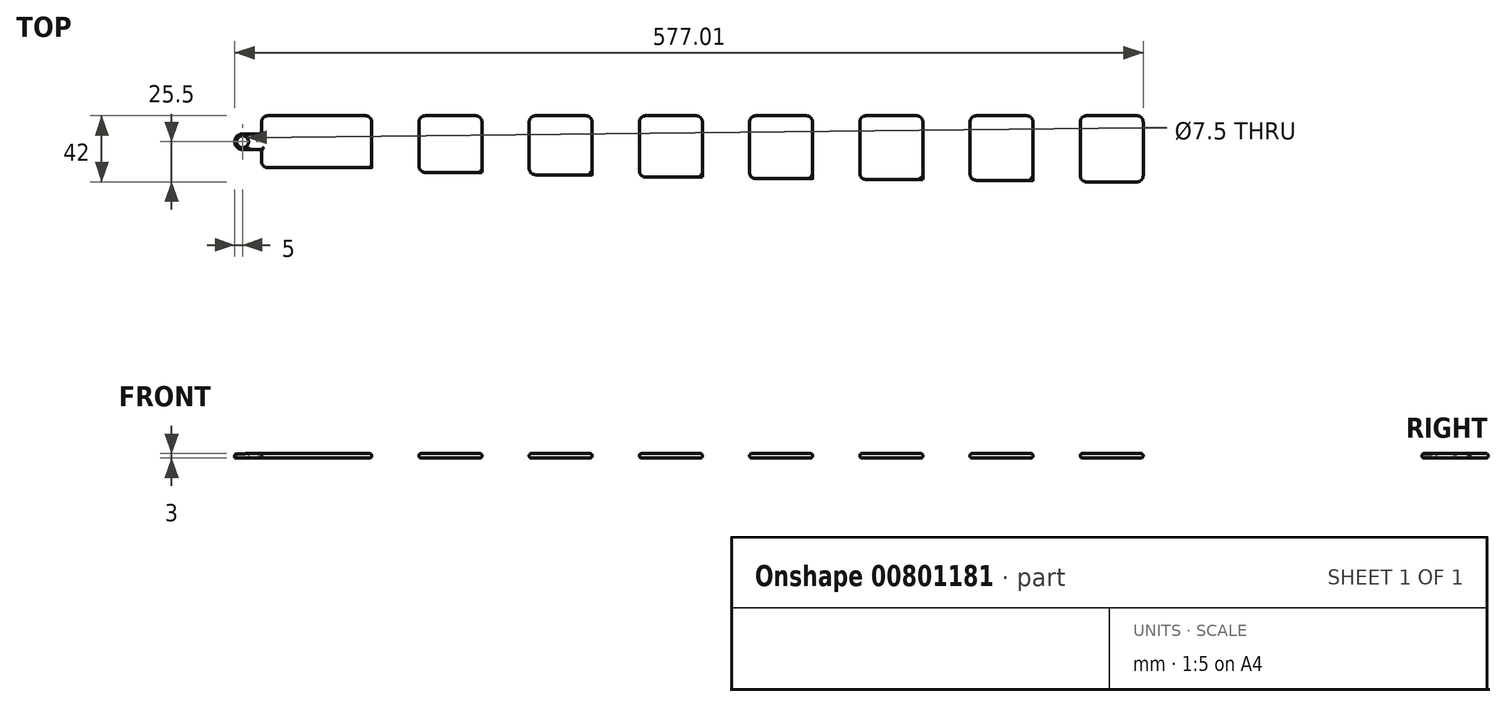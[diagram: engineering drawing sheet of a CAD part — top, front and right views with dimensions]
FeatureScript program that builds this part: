
annotation { "Feature Type Name" : "Feature", "Feature Type Description" : "" }
export const myFeature = defineFeature(function(context is Context, id is Id, definition is map)
    precondition{}
    {
        {
            var Q0;
            Q0=qCreatedBy(makeId("Top.planeOp"),FACE);
            var sketch = newSketch(context, id + "F0", { "sketchPlane" : qUnion([Q0])});
            skLineSegment(sketch, "E0.top", {"start": v(560, 0) * mm, "end": v(490, 0) * mm});
            skLineSegment(sketch, "E0.right", {"start": v(490, 1) * mm, "end": v(490, 0) * mm});
            skLineSegment(sketch, "E1.top", {"start": v(490, 1) * mm, "end": v(420, 1) * mm});
            skLineSegment(sketch, "E1.right", {"start": v(420, 1.5) * mm, "end": v(420, 1) * mm});
            skLineSegment(sketch, "E2.top", {"start": v(420, 1.5) * mm, "end": v(350, 1.5) * mm});
            skLineSegment(sketch, "E2.right", {"start": v(350, 2) * mm, "end": v(350, 1.5) * mm});
            skLineSegment(sketch, "E3.top", {"start": v(350, 2) * mm, "end": v(280, 2) * mm});
            skLineSegment(sketch, "E3.right", {"start": v(280, 3) * mm, "end": v(280, 2) * mm});
            skLineSegment(sketch, "E4.top", {"start": v(280, 3) * mm, "end": v(210, 3) * mm});
            skLineSegment(sketch, "E4.right", {"start": v(210, 4.5) * mm, "end": v(210, 3) * mm});
            skLineSegment(sketch, "E5.top", {"start": v(210, 4.5) * mm, "end": v(140, 4.5) * mm});
            skLineSegment(sketch, "E5.right", {"start": v(140, 6) * mm, "end": v(140, 4.5) * mm});
            skLineSegment(sketch, "E6", {"start": v(70, 6) * mm, "end": v(140, 6) * mm});
            skLineSegment(sketch, "E7", {"start": v(560, 0) * mm, "end": v(490, 0) * mm, "construction": true});
            skLineSegment(sketch, "E8.top", {"start": v(70, 9) * mm, "end": v(0, 9) * mm});
            skLineSegment(sketch, "E8.left", {"start": v(70, 6) * mm, "end": v(70, 9) * mm});
            skText(sketch, "E9", { "text": "9.0 6.0 4.5 3.0 2.0 1.5 1.0 0.0", "fontName": "RobotoSlab-Bold.ttf"});
            skLineSegment(sketch, "E10.bottom", {"start": v(560, 0) * mm, "end": v(0, 0) * mm, "construction": true});
            skLineSegment(sketch, "E10.left", {"start": v(560, 0) * mm, "end": v(560, 42) * mm});
            skLineSegment(sketch, "E10.right", {"start": v(0, 9) * mm, "end": v(0, 42) * mm});
            skPoint(sketch, "E11", {"position": v(-22.14, 43.86) * mm});
            skPoint(sketch, "E12", {"position": v(560, 21) * mm});
            skLineSegment(sketch, "E13.bottom", {"start": v(70, 9) * mm, "end": v(30, 9) * mm});
            skLineSegment(sketch, "E13.top", {"start": v(70, 42) * mm, "end": v(30, 42) * mm});
            skLineSegment(sketch, "E13.left", {"start": v(70, 9) * mm, "end": v(70, 42) * mm});
            skLineSegment(sketch, "E13.right", {"start": v(30, 9) * mm, "end": v(30, 42) * mm});
            skLineSegment(sketch, "E14.bottom", {"start": v(140, 6) * mm, "end": v(100, 6) * mm});
            skLineSegment(sketch, "E14.top", {"start": v(140, 42) * mm, "end": v(100, 42) * mm});
            skLineSegment(sketch, "E14.left", {"start": v(140, 6) * mm, "end": v(140, 42) * mm});
            skLineSegment(sketch, "E14.right", {"start": v(100, 6) * mm, "end": v(100, 42) * mm});
            skLineSegment(sketch, "E15.bottom", {"start": v(210, 4.5) * mm, "end": v(170, 4.5) * mm});
            skLineSegment(sketch, "E15.top", {"start": v(210, 42) * mm, "end": v(170, 42) * mm});
            skLineSegment(sketch, "E15.left", {"start": v(210, 4.5) * mm, "end": v(210, 42) * mm});
            skLineSegment(sketch, "E15.right", {"start": v(170, 4.5) * mm, "end": v(170, 42) * mm});
            skLineSegment(sketch, "E16.bottom", {"start": v(280, 3) * mm, "end": v(240, 3) * mm});
            skLineSegment(sketch, "E16.top", {"start": v(280, 42) * mm, "end": v(240, 42) * mm});
            skLineSegment(sketch, "E16.left", {"start": v(280, 3) * mm, "end": v(280, 42) * mm});
            skLineSegment(sketch, "E16.right", {"start": v(240, 3) * mm, "end": v(240, 42) * mm});
            skLineSegment(sketch, "E17.bottom", {"start": v(350, 2) * mm, "end": v(310, 2) * mm});
            skLineSegment(sketch, "E17.top", {"start": v(350, 42) * mm, "end": v(310, 42) * mm});
            skLineSegment(sketch, "E17.left", {"start": v(350, 2) * mm, "end": v(350, 42) * mm});
            skLineSegment(sketch, "E17.right", {"start": v(310, 2) * mm, "end": v(310, 42) * mm});
            skLineSegment(sketch, "E18.bottom", {"start": v(420, 1.5) * mm, "end": v(380, 1.5) * mm});
            skLineSegment(sketch, "E18.top", {"start": v(420, 42) * mm, "end": v(380, 42) * mm});
            skLineSegment(sketch, "E18.left", {"start": v(420, 1.5) * mm, "end": v(420, 42) * mm});
            skLineSegment(sketch, "E18.right", {"start": v(380, 1.5) * mm, "end": v(380, 42) * mm});
            skLineSegment(sketch, "E19.bottom", {"start": v(490, 1) * mm, "end": v(450, 1) * mm});
            skLineSegment(sketch, "E19.top", {"start": v(490, 42) * mm, "end": v(450, 42) * mm});
            skLineSegment(sketch, "E19.left", {"start": v(490, 1) * mm, "end": v(490, 42) * mm});
            skLineSegment(sketch, "E19.right", {"start": v(450, 1) * mm, "end": v(450, 42) * mm});
            skLineSegment(sketch, "E20", {"start": v(0, 42) * mm, "end": v(560, 42) * mm});
            skLineSegment(sketch, "E21.bottom", {"start": v(560, 0) * mm, "end": v(520, 0) * mm});
            skLineSegment(sketch, "E21.top", {"start": v(560, 42) * mm, "end": v(520, 42) * mm});
            skLineSegment(sketch, "E21.right", {"start": v(520, 0) * mm, "end": v(520, 42) * mm});
            const initialGuessF0  = {"E9": [-0.25714, 0.0371, 1, 0, 0.01354]};
            skSetInitialGuess(sketch, initialGuessF0);
            skSolve(sketch);
        }
        {
            var Q0;
            Q0=makeQuery(id+"F0.imprint","IMPRINT",FACE,{"disambiguationData":[TD([[makeQuery(id+"F0.imprint","IMPRINT",EDGE,{"derivedFrom":sQuery(id+"F0.wireOp",EDGE,"E8.top")}),-1.0]])]});
            var Q1;
            Q1=makeQuery(id+"F0.imprint","IMPRINT",FACE,{"disambiguationData":[TD([[makeQuery(id+"F0.imprint","IMPRINT",EDGE,{"derivedFrom":sQuery(id+"F0.wireOp",EDGE,"E6")}),1.0]])]});
            var Q2;
            Q2=makeQuery(id+"F0.imprint","IMPRINT",FACE,{"disambiguationData":[TD([[makeQuery(id+"F0.imprint","IMPRINT",EDGE,{"derivedFrom":sQuery(id+"F0.wireOp",EDGE,"E5.top")}),-1.0]])]});
            var Q3;
            Q3=makeQuery(id+"F0.imprint","IMPRINT",FACE,{"disambiguationData":[TD([[makeQuery(id+"F0.imprint","IMPRINT",EDGE,{"derivedFrom":sQuery(id+"F0.wireOp",EDGE,"E4.top")}),-1.0]])]});
            var Q4;
            Q4=makeQuery(id+"F0.imprint","IMPRINT",FACE,{"disambiguationData":[TD([[makeQuery(id+"F0.imprint","IMPRINT",EDGE,{"derivedFrom":sQuery(id+"F0.wireOp",EDGE,"E3.top")}),-1.0]])]});
            var Q5;
            Q5=makeQuery(id+"F0.imprint","IMPRINT",FACE,{"disambiguationData":[TD([[makeQuery(id+"F0.imprint","IMPRINT",EDGE,{"derivedFrom":sQuery(id+"F0.wireOp",EDGE,"E2.top")}),-1.0]])]});
            var Q6;
            Q6=makeQuery(id+"F0.imprint","IMPRINT",FACE,{"disambiguationData":[TD([[makeQuery(id+"F0.imprint","IMPRINT",EDGE,{"derivedFrom":sQuery(id+"F0.wireOp",EDGE,"E1.top")}),-1.0]])]});
            var Q7;
            Q7=makeQuery(id+"F0.imprint","IMPRINT",FACE,{"disambiguationData":[TD([[makeQuery(id+"F0.imprint","IMPRINT",EDGE,{"derivedFrom":sQuery(id+"F0.wireOp",EDGE,"E0.top")}),-1.0]])]});
            extrude(context, id + "F1", {"entities" : qUnion([Q0, Q1, Q2, Q3, Q4, Q5, Q6, Q7]), "depth" : 3 * mm, "offsetDistance" : 25 * mm});
        }
        {
            var Q0;
            Q0=makeQuery(id+"F1.opExtrude","CAP_FACE",FACE,{"disambiguationData":[OSD([sQuery(id+"F0.wireOp",EDGE,"E8.top"),sQuery(id+"F0.wireOp",EDGE,"E10.right"),sQuery(id+"F0.wireOp",EDGE,"E13.right"),sQuery(id+"F0.wireOp",EDGE,"E20")])],"isStart":false});
            var sketch = newSketch(context, id + "F2", { "sketchPlane" : qUnion([Q0])});
            skLineSegment(sketch, "E22.bottom", {"start": v(0, 30.5) * mm, "end": v(-12, 30.5) * mm});
            skLineSegment(sketch, "E22.top", {"start": v(0, 20.5) * mm, "end": v(-12, 20.5) * mm});
            skLineSegment(sketch, "E22.left", {"start": v(0, 30.5) * mm, "end": v(0, 20.5) * mm});
            skLineSegment(sketch, "E22.right", {"start": v(-17, 25.5) * mm, "end": v(-17, 25.5) * mm});
            skPoint(sketch, "E23", {"position": v(0, 25.5) * mm});
            skPoint(sketch, "E24.visualSharp", {"position": v(-17, 30.5) * mm});
            skArc(sketch, "E24.filletArc", {"start": v(-12, 30.5) * mm, "mid": v(-15.55, 29.04) * mm, "end": v(-17, 25.5) * mm});
            skPoint(sketch, "E25.visualSharp", {"position": v(-17, 20.5) * mm});
            skArc(sketch, "E25.filletArc", {"start": v(-17, 25.5) * mm, "mid": v(-15.55, 21.96) * mm, "end": v(-12, 20.5) * mm});
            skCircle(sketch, "E26", {"center": v(-12, 25.5) * mm, "radius": 3.75 * mm});
            skLineSegment(sketch, "E27.bottom", {"start": v(70, 29) * mm, "end": v(57.42, 29) * mm});
            skLineSegment(sketch, "E27.top", {"start": v(70, 19) * mm, "end": v(57.42, 19) * mm});
            skLineSegment(sketch, "E27.left", {"start": v(70, 29) * mm, "end": v(70, 19) * mm});
            skLineSegment(sketch, "E27.right", {"start": v(52.42, 24) * mm, "end": v(52.42, 24) * mm});
            skPoint(sketch, "E28", {"position": v(70, 24) * mm});
            skPoint(sketch, "E29.visualSharp", {"position": v(52.42, 29) * mm});
            skArc(sketch, "E29.filletArc", {"start": v(57.42, 29) * mm, "mid": v(53.88, 27.54) * mm, "end": v(52.42, 24) * mm});
            skPoint(sketch, "E30.visualSharp", {"position": v(52.42, 19) * mm});
            skArc(sketch, "E30.filletArc", {"start": v(52.42, 24) * mm, "mid": v(53.88, 20.46) * mm, "end": v(57.42, 19) * mm});
            skCircle(sketch, "E31", {"center": v(57.42, 24) * mm, "radius": 3.75 * mm});
            skLineSegment(sketch, "E32.bottom", {"start": v(140, 28.25) * mm, "end": v(128, 28.25) * mm});
            skLineSegment(sketch, "E32.top", {"start": v(140, 18.25) * mm, "end": v(128, 18.25) * mm});
            skLineSegment(sketch, "E32.left", {"start": v(140, 28.25) * mm, "end": v(140, 18.25) * mm});
            skLineSegment(sketch, "E32.right", {"start": v(123, 23.25) * mm, "end": v(123, 23.25) * mm});
            skPoint(sketch, "E33", {"position": v(140, 23.25) * mm});
            skPoint(sketch, "E34.visualSharp", {"position": v(123, 28.25) * mm});
            skArc(sketch, "E34.filletArc", {"start": v(128, 28.25) * mm, "mid": v(124.45, 26.79) * mm, "end": v(123, 23.25) * mm});
            skPoint(sketch, "E35.visualSharp", {"position": v(123, 18.25) * mm});
            skArc(sketch, "E35.filletArc", {"start": v(123, 23.25) * mm, "mid": v(124.45, 19.71) * mm, "end": v(128, 18.25) * mm});
            skCircle(sketch, "E36", {"center": v(128, 23.25) * mm, "radius": 3.75 * mm});
            skLineSegment(sketch, "E37.bottom", {"start": v(210, 27.5) * mm, "end": v(198, 27.5) * mm});
            skLineSegment(sketch, "E37.top", {"start": v(210, 17.5) * mm, "end": v(198, 17.5) * mm});
            skLineSegment(sketch, "E37.left", {"start": v(210, 27.5) * mm, "end": v(210, 17.5) * mm});
            skLineSegment(sketch, "E37.right", {"start": v(193, 22.5) * mm, "end": v(193, 22.5) * mm});
            skPoint(sketch, "E38", {"position": v(210, 22.5) * mm});
            skPoint(sketch, "E39.visualSharp", {"position": v(193, 27.5) * mm});
            skArc(sketch, "E39.filletArc", {"start": v(198, 27.5) * mm, "mid": v(194.45, 26.04) * mm, "end": v(193, 22.5) * mm});
            skPoint(sketch, "E40.visualSharp", {"position": v(193, 17.5) * mm});
            skArc(sketch, "E40.filletArc", {"start": v(193, 22.5) * mm, "mid": v(194.45, 18.96) * mm, "end": v(198, 17.5) * mm});
            skCircle(sketch, "E41", {"center": v(198, 22.5) * mm, "radius": 3.75 * mm});
            skLineSegment(sketch, "E42.bottom", {"start": v(280, 27) * mm, "end": v(268, 27) * mm});
            skLineSegment(sketch, "E42.top", {"start": v(280, 17) * mm, "end": v(268, 17) * mm});
            skLineSegment(sketch, "E42.left", {"start": v(280, 27) * mm, "end": v(280, 17) * mm});
            skLineSegment(sketch, "E42.right", {"start": v(263, 22) * mm, "end": v(263, 22) * mm});
            skPoint(sketch, "E43", {"position": v(280, 22) * mm});
            skPoint(sketch, "E44.visualSharp", {"position": v(263, 27) * mm});
            skArc(sketch, "E44.filletArc", {"start": v(268, 27) * mm, "mid": v(264.45, 25.54) * mm, "end": v(263, 22) * mm});
            skPoint(sketch, "E45.visualSharp", {"position": v(263, 17) * mm});
            skArc(sketch, "E45.filletArc", {"start": v(263, 22) * mm, "mid": v(264.45, 18.46) * mm, "end": v(268, 17) * mm});
            skCircle(sketch, "E46", {"center": v(268, 22) * mm, "radius": 3.75 * mm});
            skLineSegment(sketch, "E47.bottom", {"start": v(350, 26.75) * mm, "end": v(338, 26.75) * mm});
            skLineSegment(sketch, "E47.top", {"start": v(350, 16.75) * mm, "end": v(338, 16.75) * mm});
            skLineSegment(sketch, "E47.left", {"start": v(350, 26.75) * mm, "end": v(350, 16.75) * mm});
            skLineSegment(sketch, "E47.right", {"start": v(333, 21.75) * mm, "end": v(333, 21.75) * mm});
            skPoint(sketch, "E48", {"position": v(350, 21.75) * mm});
            skPoint(sketch, "E49.visualSharp", {"position": v(333, 26.75) * mm});
            skArc(sketch, "E49.filletArc", {"start": v(338, 26.75) * mm, "mid": v(334.45, 25.29) * mm, "end": v(333, 21.75) * mm});
            skPoint(sketch, "E50.visualSharp", {"position": v(333, 16.75) * mm});
            skArc(sketch, "E50.filletArc", {"start": v(333, 21.75) * mm, "mid": v(334.45, 18.21) * mm, "end": v(338, 16.75) * mm});
            skCircle(sketch, "E51", {"center": v(338, 21.75) * mm, "radius": 3.75 * mm});
            skLineSegment(sketch, "E52.bottom", {"start": v(420, 26.5) * mm, "end": v(408, 26.5) * mm});
            skLineSegment(sketch, "E52.top", {"start": v(420, 16.5) * mm, "end": v(408, 16.5) * mm});
            skLineSegment(sketch, "E52.left", {"start": v(420, 26.5) * mm, "end": v(420, 16.5) * mm});
            skLineSegment(sketch, "E52.right", {"start": v(403, 21.5) * mm, "end": v(403, 21.5) * mm});
            skPoint(sketch, "E53", {"position": v(420, 21.5) * mm});
            skPoint(sketch, "E54.visualSharp", {"position": v(403, 26.5) * mm});
            skArc(sketch, "E54.filletArc", {"start": v(408, 26.5) * mm, "mid": v(404.45, 25.04) * mm, "end": v(403, 21.5) * mm});
            skPoint(sketch, "E55.visualSharp", {"position": v(403, 16.5) * mm});
            skArc(sketch, "E55.filletArc", {"start": v(403, 21.5) * mm, "mid": v(404.45, 17.96) * mm, "end": v(408, 16.5) * mm});
            skCircle(sketch, "E56", {"center": v(408, 21.5) * mm, "radius": 3.75 * mm});
            skLineSegment(sketch, "E57.bottom", {"start": v(490, 26) * mm, "end": v(478, 26) * mm});
            skLineSegment(sketch, "E57.top", {"start": v(490, 16) * mm, "end": v(478, 16) * mm});
            skLineSegment(sketch, "E57.left", {"start": v(490, 26) * mm, "end": v(490, 16) * mm});
            skLineSegment(sketch, "E57.right", {"start": v(473, 21) * mm, "end": v(473, 21) * mm});
            skPoint(sketch, "E58", {"position": v(490, 21) * mm});
            skPoint(sketch, "E59.visualSharp", {"position": v(473, 26) * mm});
            skArc(sketch, "E59.filletArc", {"start": v(478, 26) * mm, "mid": v(474.45, 24.54) * mm, "end": v(473, 21) * mm});
            skPoint(sketch, "E60.visualSharp", {"position": v(473, 16) * mm});
            skArc(sketch, "E60.filletArc", {"start": v(473, 21) * mm, "mid": v(474.45, 17.46) * mm, "end": v(478, 16) * mm});
            skCircle(sketch, "E61", {"center": v(478, 21) * mm, "radius": 3.75 * mm});
            skSolve(sketch);
        }
        {
            var Q0;
            Q0 = qSketchRegion(id + "F2", true);
            var Q1;
            Q1=makeQuery(id+"F1.opExtrude","CAP_FACE",FACE,{"disambiguationData":[OSD([sQuery(id+"F0.wireOp",EDGE,"E8.top"),sQuery(id+"F0.wireOp",EDGE,"E10.right"),sQuery(id+"F0.wireOp",EDGE,"E13.right"),sQuery(id+"F0.wireOp",EDGE,"E20")])],"isStart":true});
            extrude(context, id + "F3", {"entities" : qUnion([Q0]), "operationType" : NewBodyOperationType.ADD, "endBound" : BoundingType.UP_TO_SURFACE, "oppositeDirection" : true, "depth" : 25 * mm, "endBoundEntityFace" : qUnion([Q1]), "offsetDistance" : 25 * mm});
        }
        {
            var Q0;
            Q0=makeQuery(id+"F1.opExtrude","SWEPT_EDGE",EDGE,{"disambiguationData":[OSD([sQuery(id+"F0.wireOp",EDGE,"E10.right"),sQuery(id+"F0.wireOp",EDGE,"E20")])]});
            var Q1;
            Q1=makeQuery(id+"F1.opExtrude","SWEPT_EDGE",EDGE,{"disambiguationData":[OSD([sQuery(id+"F0.wireOp",EDGE,"E13.right"),sQuery(id+"F0.wireOp",EDGE,"E20")])]});
            var Q2;
            Q2=makeQuery(id+"F1.opExtrude","SWEPT_EDGE",EDGE,{"disambiguationData":[OSD([sQuery(id+"F0.wireOp",EDGE,"E8.top"),sQuery(id+"F0.wireOp",EDGE,"E10.right")])]});
            var Q3;
            Q3=makeQuery(id+"F1.opExtrude","SWEPT_EDGE",EDGE,{"disambiguationData":[OSD([sQuery(id+"F0.wireOp",EDGE,"E8.top"),sQuery(id+"F0.wireOp",EDGE,"E13.bottom"),sQuery(id+"F0.wireOp",EDGE,"E13.right")])]});
            var Q4;
            Q4=makeQuery(id+"F1.opExtrude","SWEPT_EDGE",EDGE,{"disambiguationData":[OSD([sQuery(id+"F0.wireOp",EDGE,"E13.left"),sQuery(id+"F0.wireOp",EDGE,"E20")])]});
            var Q5;
            Q5=makeQuery(id+"F1.opExtrude","SWEPT_EDGE",EDGE,{"disambiguationData":[OSD([sQuery(id+"F0.wireOp",EDGE,"E14.left"),sQuery(id+"F0.wireOp",EDGE,"E20")])]});
            var Q6;
            Q6=makeQuery(id+"F1.opExtrude","SWEPT_EDGE",EDGE,{"disambiguationData":[OSD([sQuery(id+"F0.wireOp",EDGE,"E19.left"),sQuery(id+"F0.wireOp",EDGE,"E20")])]});
            var Q7;
            Q7=makeQuery(id+"F1.opExtrude","SWEPT_EDGE",EDGE,{"disambiguationData":[OSD([sQuery(id+"F0.wireOp",EDGE,"E18.left"),sQuery(id+"F0.wireOp",EDGE,"E20")])]});
            var Q8;
            Q8=makeQuery(id+"F1.opExtrude","SWEPT_EDGE",EDGE,{"disambiguationData":[OSD([sQuery(id+"F0.wireOp",EDGE,"E17.left"),sQuery(id+"F0.wireOp",EDGE,"E20")])]});
            var Q9;
            Q9=makeQuery(id+"F1.opExtrude","SWEPT_EDGE",EDGE,{"disambiguationData":[OSD([sQuery(id+"F0.wireOp",EDGE,"E16.left"),sQuery(id+"F0.wireOp",EDGE,"E20")])]});
            var Q10;
            Q10=makeQuery(id+"F1.opExtrude","SWEPT_EDGE",EDGE,{"disambiguationData":[OSD([sQuery(id+"F0.wireOp",EDGE,"E15.left"),sQuery(id+"F0.wireOp",EDGE,"E20")])]});
            var Q11;
            Q11=makeQuery(id+"F1.opExtrude","SWEPT_EDGE",EDGE,{"disambiguationData":[OSD([sQuery(id+"F0.wireOp",EDGE,"E20"),sQuery(id+"F0.wireOp",EDGE,"E21.top"),sQuery(id+"F0.wireOp",EDGE,"E21.right")])]});
            var Q12;
            Q12=makeQuery(id+"F1.opExtrude","SWEPT_EDGE",EDGE,{"disambiguationData":[OSD([sQuery(id+"F0.wireOp",EDGE,"E19.right"),sQuery(id+"F0.wireOp",EDGE,"E20")])]});
            var Q13;
            Q13=makeQuery(id+"F1.opExtrude","SWEPT_EDGE",EDGE,{"disambiguationData":[OSD([sQuery(id+"F0.wireOp",EDGE,"E18.right"),sQuery(id+"F0.wireOp",EDGE,"E20")])]});
            var Q14;
            Q14=makeQuery(id+"F1.opExtrude","SWEPT_EDGE",EDGE,{"disambiguationData":[OSD([sQuery(id+"F0.wireOp",EDGE,"E17.right"),sQuery(id+"F0.wireOp",EDGE,"E20")])]});
            var Q15;
            Q15=makeQuery(id+"F1.opExtrude","SWEPT_EDGE",EDGE,{"disambiguationData":[OSD([sQuery(id+"F0.wireOp",EDGE,"E16.right"),sQuery(id+"F0.wireOp",EDGE,"E20")])]});
            var Q16;
            Q16=makeQuery(id+"F1.opExtrude","SWEPT_EDGE",EDGE,{"disambiguationData":[OSD([sQuery(id+"F0.wireOp",EDGE,"E15.right"),sQuery(id+"F0.wireOp",EDGE,"E20")])]});
            var Q17;
            Q17=makeQuery(id+"F1.opExtrude","SWEPT_EDGE",EDGE,{"disambiguationData":[OSD([sQuery(id+"F0.wireOp",EDGE,"E14.right"),sQuery(id+"F0.wireOp",EDGE,"E20")])]});
            var Q18;
            Q18=makeQuery(id+"F1.opExtrude","SWEPT_EDGE",EDGE,{"disambiguationData":[OSD([sQuery(id+"F0.wireOp",EDGE,"E6"),sQuery(id+"F0.wireOp",EDGE,"E14.bottom"),sQuery(id+"F0.wireOp",EDGE,"E14.right")])]});
            var Q19;
            Q19=makeQuery(id+"F1.opExtrude","SWEPT_EDGE",EDGE,{"disambiguationData":[OSD([sQuery(id+"F0.wireOp",EDGE,"E5.top"),sQuery(id+"F0.wireOp",EDGE,"E15.bottom"),sQuery(id+"F0.wireOp",EDGE,"E15.right")])]});
            var Q20;
            Q20=makeQuery(id+"F1.opExtrude","SWEPT_EDGE",EDGE,{"disambiguationData":[OSD([sQuery(id+"F0.wireOp",EDGE,"E4.top"),sQuery(id+"F0.wireOp",EDGE,"E16.bottom"),sQuery(id+"F0.wireOp",EDGE,"E16.right")])]});
            var Q21;
            Q21=makeQuery(id+"F1.opExtrude","SWEPT_EDGE",EDGE,{"disambiguationData":[OSD([sQuery(id+"F0.wireOp",EDGE,"E3.top"),sQuery(id+"F0.wireOp",EDGE,"E17.bottom"),sQuery(id+"F0.wireOp",EDGE,"E17.right")])]});
            var Q22;
            Q22=makeQuery(id+"F1.opExtrude","SWEPT_EDGE",EDGE,{"disambiguationData":[OSD([sQuery(id+"F0.wireOp",EDGE,"E2.top"),sQuery(id+"F0.wireOp",EDGE,"E18.bottom"),sQuery(id+"F0.wireOp",EDGE,"E18.right")])]});
            var Q23;
            Q23=makeQuery(id+"F1.opExtrude","SWEPT_EDGE",EDGE,{"disambiguationData":[OSD([sQuery(id+"F0.wireOp",EDGE,"E1.top"),sQuery(id+"F0.wireOp",EDGE,"E19.bottom"),sQuery(id+"F0.wireOp",EDGE,"E19.right")])]});
            var Q24;
            Q24=makeQuery(id+"F1.opExtrude","SWEPT_EDGE",EDGE,{"disambiguationData":[OSD([sQuery(id+"F0.wireOp",EDGE,"E0.top"),sQuery(id+"F0.wireOp",EDGE,"E21.bottom"),sQuery(id+"F0.wireOp",EDGE,"E21.right")])]});
            var Q25;
            Q25=makeQuery(id+"F1.opExtrude","SWEPT_EDGE",EDGE,{"disambiguationData":[OSD([sQuery(id+"F0.wireOp",EDGE,"E6"),sQuery(id+"F0.wireOp",EDGE,"E8.left")])]});
            var Q26;
            Q26=makeQuery(id+"F1.opExtrude","SWEPT_EDGE",EDGE,{"disambiguationData":[OSD([sQuery(id+"F0.wireOp",EDGE,"E5.top"),sQuery(id+"F0.wireOp",EDGE,"E5.right")])]});
            var Q27;
            Q27=makeQuery(id+"F1.opExtrude","SWEPT_EDGE",EDGE,{"disambiguationData":[OSD([sQuery(id+"F0.wireOp",EDGE,"E4.top"),sQuery(id+"F0.wireOp",EDGE,"E4.right")])]});
            var Q28;
            Q28=makeQuery(id+"F1.opExtrude","SWEPT_EDGE",EDGE,{"disambiguationData":[OSD([sQuery(id+"F0.wireOp",EDGE,"E3.top"),sQuery(id+"F0.wireOp",EDGE,"E3.right")])]});
            var Q29;
            Q29=makeQuery(id+"F1.opExtrude","SWEPT_EDGE",EDGE,{"disambiguationData":[OSD([sQuery(id+"F0.wireOp",EDGE,"E2.top"),sQuery(id+"F0.wireOp",EDGE,"E2.right")])]});
            var Q30;
            Q30=makeQuery(id+"F1.opExtrude","SWEPT_EDGE",EDGE,{"disambiguationData":[OSD([sQuery(id+"F0.wireOp",EDGE,"E1.top"),sQuery(id+"F0.wireOp",EDGE,"E1.right")])]});
            var Q31;
            Q31=makeQuery(id+"F1.opExtrude","SWEPT_EDGE",EDGE,{"disambiguationData":[OSD([sQuery(id+"F0.wireOp",EDGE,"E0.top"),sQuery(id+"F0.wireOp",EDGE,"E0.right")])]});
            fillet(context, id + "F4", {"entities" : qUnion([Q0, Q1, Q2, Q3, Q4, Q5, Q6, Q7, Q8, Q9, Q10, Q11, Q12, Q13, Q14, Q15, Q16, Q17, Q18, Q19, Q20, Q21, Q22, Q23, Q24, Q25, Q26, Q27, Q28, Q29, Q30, Q31]), "radius" : 4 * mm, "tangentPropagation" : true, "allowEdgeOverflow" : false});
        }
        {
            var Q0;
            {var subQ1=sQuery(id+"F0.wireOp",EDGE,"E18.left");var subQ2=sQuery(id+"F0.wireOp",EDGE,"E1.right");var subQ3=sQuery(id+"F0.wireOp",EDGE,"E1.top");Q0=makeQuery(id+"F3.boolean.opBoolean","SPLIT",EDGE,{"disambiguationData":[TD([makeQuery(id+"F1.opExtrude","SWEPT_FACE",FACE,{"disambiguationData":[OSD([subQ3])]})])],"derivedFrom":makeQuery(id+"F1.opExtrude","CAP_EDGE",EDGE,{"disambiguationData":[OSD([subQ2,subQ1])],"isStart":false})});}
            var Q1;
            Q1=makeQuery(id+"F3.opExtrude","CAP_EDGE",EDGE,{"disambiguationData":[OSD([sQuery(id+"F2.wireOp",EDGE,"E54.filletArc"),sQuery(id+"F2.wireOp",EDGE,"E55.filletArc")])],"isStart":true});
            var Q2;
            Q2=makeQuery(id+"F3.opExtrude","CAP_EDGE",EDGE,{"disambiguationData":[OSD([sQuery(id+"F2.wireOp",EDGE,"E34.filletArc"),sQuery(id+"F2.wireOp",EDGE,"E35.filletArc")])],"isStart":true});
            var Q3;
            {var subQ1=sQuery(id+"F0.wireOp",EDGE,"E5.top");var subQ2=sQuery(id+"F0.wireOp",EDGE,"E14.left");var subQ3=sQuery(id+"F0.wireOp",EDGE,"E5.right");Q3=makeQuery(id+"F3.boolean.opBoolean","SPLIT",EDGE,{"disambiguationData":[TD([makeQuery(id+"F1.opExtrude","SWEPT_FACE",FACE,{"disambiguationData":[OSD([subQ1])]})])],"derivedFrom":makeQuery(id+"F1.opExtrude","CAP_EDGE",EDGE,{"disambiguationData":[OSD([subQ3,subQ2])],"isStart":false})});}
            var Q4;
            {var subQ1=sQuery(id+"F0.wireOp",EDGE,"E17.left");var subQ2=sQuery(id+"F0.wireOp",EDGE,"E2.right");var subQ3=sQuery(id+"F0.wireOp",EDGE,"E2.top");Q4=makeQuery(id+"F3.boolean.opBoolean","SPLIT",EDGE,{"disambiguationData":[TD([makeQuery(id+"F1.opExtrude","SWEPT_FACE",FACE,{"disambiguationData":[OSD([subQ3])]})])],"derivedFrom":makeQuery(id+"F1.opExtrude","CAP_EDGE",EDGE,{"disambiguationData":[OSD([subQ2,subQ1])],"isStart":false})});}
            var Q5;
            Q5=makeQuery(id+"F3.opExtrude","CAP_EDGE",EDGE,{"disambiguationData":[OSD([sQuery(id+"F2.wireOp",EDGE,"E59.filletArc"),sQuery(id+"F2.wireOp",EDGE,"E60.filletArc")])],"isStart":true});
            var Q6;
            {var subQ1=sQuery(id+"F0.wireOp",EDGE,"E19.left");var subQ2=sQuery(id+"F0.wireOp",EDGE,"E0.right");var subQ3=sQuery(id+"F0.wireOp",EDGE,"E0.top");Q6=makeQuery(id+"F3.boolean.opBoolean","SPLIT",EDGE,{"disambiguationData":[TD([makeQuery(id+"F1.opExtrude","SWEPT_FACE",FACE,{"disambiguationData":[OSD([subQ3])]})])],"derivedFrom":makeQuery(id+"F1.opExtrude","CAP_EDGE",EDGE,{"disambiguationData":[OSD([subQ2,subQ1])],"isStart":false})});}
            var Q7;
            {var subQ1=sQuery(id+"F0.wireOp",EDGE,"E13.left");var subQ2=sQuery(id+"F0.wireOp",EDGE,"E8.left");var subQ3=sQuery(id+"F0.wireOp",EDGE,"E6");Q7=makeQuery(id+"F3.boolean.opBoolean","SPLIT",EDGE,{"disambiguationData":[TD([makeQuery(id+"F1.opExtrude","SWEPT_FACE",FACE,{"disambiguationData":[OSD([subQ3])]})])],"derivedFrom":makeQuery(id+"F1.opExtrude","CAP_EDGE",EDGE,{"disambiguationData":[OSD([subQ2,subQ1])],"isStart":false})});}
            var Q8;
            Q8=makeQuery(id+"F3.opExtrude","CAP_EDGE",EDGE,{"disambiguationData":[OSD([sQuery(id+"F2.wireOp",EDGE,"E39.filletArc"),sQuery(id+"F2.wireOp",EDGE,"E40.filletArc")])],"isStart":true});
            var Q9;
            {var subQ1=sQuery(id+"F0.wireOp",EDGE,"E15.left");var subQ2=sQuery(id+"F0.wireOp",EDGE,"E4.right");var subQ3=sQuery(id+"F0.wireOp",EDGE,"E4.top");Q9=makeQuery(id+"F3.boolean.opBoolean","SPLIT",EDGE,{"disambiguationData":[TD([makeQuery(id+"F1.opExtrude","SWEPT_FACE",FACE,{"disambiguationData":[OSD([subQ3])]})])],"derivedFrom":makeQuery(id+"F1.opExtrude","CAP_EDGE",EDGE,{"disambiguationData":[OSD([subQ2,subQ1])],"isStart":false})});}
            var Q10;
            Q10=makeQuery(id+"F3.opExtrude","CAP_EDGE",EDGE,{"disambiguationData":[OSD([sQuery(id+"F2.wireOp",EDGE,"E24.filletArc"),sQuery(id+"F2.wireOp",EDGE,"E25.filletArc")])],"isStart":true});
            var Q11;
            {var subQ1=sQuery(id+"F0.wireOp",EDGE,"E16.left");var subQ2=sQuery(id+"F0.wireOp",EDGE,"E3.right");var subQ3=sQuery(id+"F0.wireOp",EDGE,"E3.top");Q11=makeQuery(id+"F3.boolean.opBoolean","SPLIT",EDGE,{"disambiguationData":[TD([makeQuery(id+"F1.opExtrude","SWEPT_FACE",FACE,{"disambiguationData":[OSD([subQ3])]})])],"derivedFrom":makeQuery(id+"F1.opExtrude","CAP_EDGE",EDGE,{"disambiguationData":[OSD([subQ2,subQ1])],"isStart":false})});}
            var Q12;
            Q12=makeQuery(id+"F1.opExtrude","CAP_EDGE",EDGE,{"disambiguationData":[OSD([sQuery(id+"F0.wireOp",EDGE,"E19.right")])],"isStart":false});
            var Q13;
            Q13=makeQuery(id+"F1.opExtrude","SWEPT_EDGE",EDGE,{"disambiguationData":[OSD([sQuery(id+"F0.wireOp",EDGE,"E1.top"),sQuery(id+"F0.wireOp",EDGE,"E1.right")])]});
            var Q14;
            {var subQ0=sQuery(id+"F0.wireOp",EDGE,"E20");Q14=makeQuery(id+"F1.opExtrude","CAP_EDGE",EDGE,{"disambiguationData":[OSD([subQ0]),TDD([makeQuery(id+"F0.imprint","IMPRINT",EDGE,{"disambiguationData":[TD([[makeQuery(id+"F0.imprint","INTERSECT",VERTEX,{"derivedFrom":[sQuery(id+"F0.wireOp",EDGE,"E18.left"),subQ0]}),-1.0]])],"derivedFrom":subQ0})])],"isStart":false});}
            var Q15;
            Q15=makeQuery(id+"F3.opExtrude","SWEPT_EDGE",EDGE,{"disambiguationData":[OSD([sQuery(id+"F2.wireOp",EDGE,"E52.bottom"),sQuery(id+"F2.wireOp",EDGE,"E54.filletArc")])]});
            var Q16;
            Q16=makeQuery(id+"F3.opExtrude","CAP_EDGE",EDGE,{"disambiguationData":[OSD([sQuery(id+"F2.wireOp",EDGE,"E56")])],"isStart":true});
            var Q17;
            Q17=makeQuery(id+"F3.opExtrude","CAP_EDGE",EDGE,{"disambiguationData":[OSD([sQuery(id+"F2.wireOp",EDGE,"E52.top")])],"isStart":true});
            var Q18;
            {var subQ1=sQuery(id+"F0.wireOp",EDGE,"E18.left");var subQ3=sQuery(id+"F0.wireOp",EDGE,"E1.right");var subQ4=sQuery(id+"F2.wireOp",EDGE,"E52.bottom");Q18=makeQuery(id+"F3.boolean.opBoolean","SPLIT",EDGE,{"disambiguationData":[TD([makeQuery(id+"F3.opExtrude","SWEPT_FACE",FACE,{"disambiguationData":[OSD([subQ4])]})])],"derivedFrom":makeQuery(id+"F1.opExtrude","CAP_EDGE",EDGE,{"disambiguationData":[OSD([subQ3,subQ1])],"isStart":false})});}
            var Q19;
            Q19=makeQuery(id+"F3.opExtrude","CAP_EDGE",EDGE,{"disambiguationData":[OSD([sQuery(id+"F2.wireOp",EDGE,"E52.bottom")])],"isStart":true});
            var Q20;
            Q20=makeQuery(id+"F1.opExtrude","SWEPT_EDGE",EDGE,{"disambiguationData":[OSD([sQuery(id+"F0.wireOp",EDGE,"E5.top"),sQuery(id+"F0.wireOp",EDGE,"E5.right")])]});
            var Q21;
            {var subQ0=sQuery(id+"F0.wireOp",EDGE,"E20");Q21=makeQuery(id+"F1.opExtrude","CAP_EDGE",EDGE,{"disambiguationData":[OSD([subQ0]),TDD([makeQuery(id+"F0.imprint","IMPRINT",EDGE,{"disambiguationData":[TD([[makeQuery(id+"F0.imprint","INTERSECT",VERTEX,{"derivedFrom":[sQuery(id+"F0.wireOp",EDGE,"E14.left"),subQ0]}),-1.0]])],"derivedFrom":subQ0})])],"isStart":false});}
            var Q22;
            Q22=makeQuery(id+"F1.opExtrude","CAP_EDGE",EDGE,{"disambiguationData":[OSD([sQuery(id+"F0.wireOp",EDGE,"E5.top")])],"isStart":false});
            var Q23;
            Q23=makeQuery(id+"F1.opExtrude","CAP_EDGE",EDGE,{"disambiguationData":[OSD([sQuery(id+"F0.wireOp",EDGE,"E15.right")])],"isStart":false});
            var Q24;
            Q24=makeQuery(id+"F3.opExtrude","SWEPT_EDGE",EDGE,{"disambiguationData":[OSD([sQuery(id+"F2.wireOp",EDGE,"E32.top"),sQuery(id+"F2.wireOp",EDGE,"E35.filletArc")])]});
            var Q25;
            Q25=makeQuery(id+"F3.opExtrude","SWEPT_EDGE",EDGE,{"disambiguationData":[OSD([sQuery(id+"F2.wireOp",EDGE,"E32.bottom"),sQuery(id+"F2.wireOp",EDGE,"E34.filletArc")])]});
            var Q26;
            Q26=makeQuery(id+"F3.opExtrude","CAP_EDGE",EDGE,{"disambiguationData":[OSD([sQuery(id+"F2.wireOp",EDGE,"E32.top")])],"isStart":true});
            var Q27;
            {var subQ1=sQuery(id+"F0.wireOp",EDGE,"E14.left");var subQ3=sQuery(id+"F2.wireOp",EDGE,"E32.bottom");var subQ4=sQuery(id+"F0.wireOp",EDGE,"E5.right");Q27=makeQuery(id+"F3.boolean.opBoolean","SPLIT",EDGE,{"disambiguationData":[TD([makeQuery(id+"F3.opExtrude","SWEPT_FACE",FACE,{"disambiguationData":[OSD([subQ3])]})])],"derivedFrom":makeQuery(id+"F1.opExtrude","CAP_EDGE",EDGE,{"disambiguationData":[OSD([subQ4,subQ1])],"isStart":false})});}
            var Q28;
            Q28=makeQuery(id+"F3.opExtrude","CAP_EDGE",EDGE,{"disambiguationData":[OSD([sQuery(id+"F2.wireOp",EDGE,"E32.bottom")])],"isStart":true});
            var Q29;
            Q29=makeQuery(id+"F3.opExtrude","CAP_EDGE",EDGE,{"disambiguationData":[OSD([sQuery(id+"F2.wireOp",EDGE,"E36")])],"isStart":true});
            var Q30;
            Q30=makeQuery(id+"F1.opExtrude","CAP_EDGE",EDGE,{"disambiguationData":[OSD([sQuery(id+"F0.wireOp",EDGE,"E2.top")])],"isStart":false});
            var Q31;
            {var subQ0=sQuery(id+"F0.wireOp",EDGE,"E20");Q31=makeQuery(id+"F1.opExtrude","CAP_EDGE",EDGE,{"disambiguationData":[OSD([subQ0]),TDD([makeQuery(id+"F0.imprint","IMPRINT",EDGE,{"disambiguationData":[TD([[makeQuery(id+"F0.imprint","INTERSECT",VERTEX,{"derivedFrom":[sQuery(id+"F0.wireOp",EDGE,"E17.left"),subQ0]}),-1.0]])],"derivedFrom":subQ0})])],"isStart":false});}
            var Q32;
            Q32=makeQuery(id+"F1.opExtrude","CAP_EDGE",EDGE,{"disambiguationData":[OSD([sQuery(id+"F0.wireOp",EDGE,"E18.right")])],"isStart":false});
            var Q33;
            Q33=makeQuery(id+"F1.opExtrude","SWEPT_EDGE",EDGE,{"disambiguationData":[OSD([sQuery(id+"F0.wireOp",EDGE,"E2.top"),sQuery(id+"F0.wireOp",EDGE,"E2.right")])]});
            var Q34;
            Q34=makeQuery(id+"F3.opExtrude","CAP_EDGE",EDGE,{"disambiguationData":[OSD([sQuery(id+"F2.wireOp",EDGE,"E51")])],"isStart":true});
            var Q35;
            {var subQ1=sQuery(id+"F0.wireOp",EDGE,"E17.left");var subQ3=sQuery(id+"F0.wireOp",EDGE,"E2.right");var subQ4=sQuery(id+"F2.wireOp",EDGE,"E47.bottom");Q35=makeQuery(id+"F3.boolean.opBoolean","SPLIT",EDGE,{"disambiguationData":[TD([makeQuery(id+"F3.opExtrude","SWEPT_FACE",FACE,{"disambiguationData":[OSD([subQ4])]})])],"derivedFrom":makeQuery(id+"F1.opExtrude","CAP_EDGE",EDGE,{"disambiguationData":[OSD([subQ3,subQ1])],"isStart":false})});}
            var Q36;
            Q36=makeQuery(id+"F3.opExtrude","CAP_EDGE",EDGE,{"disambiguationData":[OSD([sQuery(id+"F2.wireOp",EDGE,"E49.filletArc"),sQuery(id+"F2.wireOp",EDGE,"E50.filletArc")])],"isStart":true});
            var Q37;
            Q37=makeQuery(id+"F3.opExtrude","CAP_EDGE",EDGE,{"disambiguationData":[OSD([sQuery(id+"F2.wireOp",EDGE,"E47.bottom")])],"isStart":true});
            var Q38;
            Q38=makeQuery(id+"F3.opExtrude","CAP_EDGE",EDGE,{"disambiguationData":[OSD([sQuery(id+"F2.wireOp",EDGE,"E47.top")])],"isStart":true});
            var Q39;
            Q39=makeQuery(id+"F1.opExtrude","SWEPT_EDGE",EDGE,{"disambiguationData":[OSD([sQuery(id+"F0.wireOp",EDGE,"E0.top"),sQuery(id+"F0.wireOp",EDGE,"E0.right")])]});
            var Q40;
            Q40=makeQuery(id+"F1.opExtrude","CAP_EDGE",EDGE,{"disambiguationData":[OSD([sQuery(id+"F0.wireOp",EDGE,"E21.right")])],"isStart":false});
            var Q41;
            {var subQ0=sQuery(id+"F0.wireOp",EDGE,"E20");Q41=makeQuery(id+"F1.opExtrude","CAP_EDGE",EDGE,{"disambiguationData":[OSD([subQ0]),TDD([makeQuery(id+"F0.imprint","IMPRINT",EDGE,{"disambiguationData":[TD([[makeQuery(id+"F0.imprint","INTERSECT",VERTEX,{"derivedFrom":[sQuery(id+"F0.wireOp",EDGE,"E19.left"),subQ0]}),-1.0]])],"derivedFrom":subQ0})])],"isStart":false});}
            var Q42;
            Q42=makeQuery(id+"F3.opExtrude","CAP_EDGE",EDGE,{"disambiguationData":[OSD([sQuery(id+"F2.wireOp",EDGE,"E61")])],"isStart":true});
            var Q43;
            Q43=makeQuery(id+"F3.opExtrude","CAP_EDGE",EDGE,{"disambiguationData":[OSD([sQuery(id+"F2.wireOp",EDGE,"E57.top")])],"isStart":true});
            var Q44;
            {var subQ1=sQuery(id+"F0.wireOp",EDGE,"E19.left");var subQ3=sQuery(id+"F0.wireOp",EDGE,"E0.right");var subQ4=sQuery(id+"F2.wireOp",EDGE,"E57.bottom");Q44=makeQuery(id+"F3.boolean.opBoolean","SPLIT",EDGE,{"disambiguationData":[TD([makeQuery(id+"F3.opExtrude","SWEPT_FACE",FACE,{"disambiguationData":[OSD([subQ4])]})])],"derivedFrom":makeQuery(id+"F1.opExtrude","CAP_EDGE",EDGE,{"disambiguationData":[OSD([subQ3,subQ1])],"isStart":false})});}
            var Q45;
            Q45=makeQuery(id+"F3.opExtrude","SWEPT_EDGE",EDGE,{"disambiguationData":[OSD([sQuery(id+"F2.wireOp",EDGE,"E57.top"),sQuery(id+"F2.wireOp",EDGE,"E60.filletArc")])]});
            var Q46;
            Q46=makeQuery(id+"F3.opExtrude","CAP_EDGE",EDGE,{"disambiguationData":[OSD([sQuery(id+"F2.wireOp",EDGE,"E57.bottom")])],"isStart":true});
            var Q47;
            Q47=makeQuery(id+"F3.opExtrude","CAP_EDGE",EDGE,{"disambiguationData":[OSD([sQuery(id+"F2.wireOp",EDGE,"E27.top")])],"isStart":true});
            var Q48;
            Q48=makeQuery(id+"F3.opExtrude","CAP_EDGE",EDGE,{"disambiguationData":[OSD([sQuery(id+"F2.wireOp",EDGE,"E29.filletArc"),sQuery(id+"F2.wireOp",EDGE,"E30.filletArc")])],"isStart":true});
            var Q49;
            Q49=makeQuery(id+"F1.opExtrude","SWEPT_EDGE",EDGE,{"disambiguationData":[OSD([sQuery(id+"F0.wireOp",EDGE,"E6"),sQuery(id+"F0.wireOp",EDGE,"E8.left")])]});
            var Q50;
            {var subQ0=sQuery(id+"F0.wireOp",EDGE,"E20");Q50=makeQuery(id+"F1.opExtrude","CAP_EDGE",EDGE,{"disambiguationData":[OSD([subQ0]),TDD([makeQuery(id+"F0.imprint","IMPRINT",EDGE,{"disambiguationData":[TD([[makeQuery(id+"F0.imprint","INTERSECT",VERTEX,{"derivedFrom":[sQuery(id+"F0.wireOp",EDGE,"E13.left"),subQ0]}),-1.0]])],"derivedFrom":subQ0})])],"isStart":false});}
            var Q51;
            Q51=makeQuery(id+"F1.opExtrude","CAP_EDGE",EDGE,{"disambiguationData":[OSD([sQuery(id+"F0.wireOp",EDGE,"E14.right")])],"isStart":false});
            var Q52;
            Q52=makeQuery(id+"F3.opExtrude","CAP_EDGE",EDGE,{"disambiguationData":[OSD([sQuery(id+"F2.wireOp",EDGE,"E31")])],"isStart":true});
            var Q53;
            Q53=makeQuery(id+"F3.opExtrude","CAP_EDGE",EDGE,{"disambiguationData":[OSD([sQuery(id+"F2.wireOp",EDGE,"E27.bottom")])],"isStart":true});
            var Q54;
            {var subQ1=sQuery(id+"F0.wireOp",EDGE,"E13.left");var subQ3=sQuery(id+"F0.wireOp",EDGE,"E8.left");var subQ4=sQuery(id+"F2.wireOp",EDGE,"E27.bottom");Q54=makeQuery(id+"F3.boolean.opBoolean","SPLIT",EDGE,{"disambiguationData":[TD([makeQuery(id+"F3.opExtrude","SWEPT_FACE",FACE,{"disambiguationData":[OSD([subQ4])]})])],"derivedFrom":makeQuery(id+"F1.opExtrude","CAP_EDGE",EDGE,{"disambiguationData":[OSD([subQ3,subQ1])],"isStart":false})});}
            var Q55;
            Q55=makeQuery(id+"F1.opExtrude","CAP_EDGE",EDGE,{"disambiguationData":[OSD([sQuery(id+"F0.wireOp",EDGE,"E4.top")])],"isStart":false});
            var Q56;
            {var subQ0=sQuery(id+"F0.wireOp",EDGE,"E20");Q56=makeQuery(id+"F1.opExtrude","CAP_EDGE",EDGE,{"disambiguationData":[OSD([subQ0]),TDD([makeQuery(id+"F0.imprint","IMPRINT",EDGE,{"disambiguationData":[TD([[makeQuery(id+"F0.imprint","INTERSECT",VERTEX,{"derivedFrom":[sQuery(id+"F0.wireOp",EDGE,"E15.left"),subQ0]}),-1.0]])],"derivedFrom":subQ0})])],"isStart":false});}
            var Q57;
            Q57=makeQuery(id+"F1.opExtrude","CAP_EDGE",EDGE,{"disambiguationData":[OSD([sQuery(id+"F0.wireOp",EDGE,"E16.right")])],"isStart":false});
            var Q58;
            Q58=makeQuery(id+"F1.opExtrude","SWEPT_EDGE",EDGE,{"disambiguationData":[OSD([sQuery(id+"F0.wireOp",EDGE,"E4.top"),sQuery(id+"F0.wireOp",EDGE,"E4.right")])]});
            var Q59;
            Q59=makeQuery(id+"F3.opExtrude","CAP_EDGE",EDGE,{"disambiguationData":[OSD([sQuery(id+"F2.wireOp",EDGE,"E37.bottom")])],"isStart":true});
            var Q60;
            Q60=makeQuery(id+"F3.opExtrude","CAP_EDGE",EDGE,{"disambiguationData":[OSD([sQuery(id+"F2.wireOp",EDGE,"E41")])],"isStart":true});
            var Q61;
            {var subQ1=sQuery(id+"F0.wireOp",EDGE,"E15.left");var subQ3=sQuery(id+"F0.wireOp",EDGE,"E4.right");var subQ4=sQuery(id+"F2.wireOp",EDGE,"E37.bottom");Q61=makeQuery(id+"F3.boolean.opBoolean","SPLIT",EDGE,{"disambiguationData":[TD([makeQuery(id+"F3.opExtrude","SWEPT_FACE",FACE,{"disambiguationData":[OSD([subQ4])]})])],"derivedFrom":makeQuery(id+"F1.opExtrude","CAP_EDGE",EDGE,{"disambiguationData":[OSD([subQ3,subQ1])],"isStart":false})});}
            var Q62;
            Q62=makeQuery(id+"F3.opExtrude","CAP_EDGE",EDGE,{"disambiguationData":[OSD([sQuery(id+"F2.wireOp",EDGE,"E37.top")])],"isStart":true});
            var Q63;
            Q63=makeQuery(id+"F3.opExtrude","SWEPT_EDGE",EDGE,{"disambiguationData":[OSD([sQuery(id+"F2.wireOp",EDGE,"E37.bottom"),sQuery(id+"F2.wireOp",EDGE,"E39.filletArc")])]});
            var Q64;
            {var subQ1=sQuery(id+"F0.wireOp",EDGE,"E10.right");var subQ2=sQuery(id+"F0.wireOp",EDGE,"E8.top");Q64=makeQuery(id+"F3.boolean.opBoolean","SPLIT",EDGE,{"disambiguationData":[TD([makeQuery(id+"F1.opExtrude","SWEPT_FACE",FACE,{"disambiguationData":[OSD([subQ2])]})])],"derivedFrom":makeQuery(id+"F1.opExtrude","CAP_EDGE",EDGE,{"disambiguationData":[OSD([subQ1])],"isStart":false})});}
            var Q65;
            {var subQ0=sQuery(id+"F0.wireOp",EDGE,"E20");Q65=makeQuery(id+"F1.opExtrude","CAP_EDGE",EDGE,{"disambiguationData":[OSD([subQ0]),TDD([makeQuery(id+"F0.imprint","IMPRINT",EDGE,{"disambiguationData":[TD([[makeQuery(id+"F0.imprint","INTERSECT",VERTEX,{"derivedFrom":[sQuery(id+"F0.wireOp",EDGE,"E10.right"),subQ0]}),-1.0]])],"derivedFrom":subQ0})])],"isStart":false});}
            var Q66;
            Q66=makeQuery(id+"F1.opExtrude","CAP_EDGE",EDGE,{"disambiguationData":[OSD([sQuery(id+"F0.wireOp",EDGE,"E13.right")])],"isStart":false});
            var Q67;
            Q67=makeQuery(id+"F3.opExtrude","CAP_EDGE",EDGE,{"disambiguationData":[OSD([sQuery(id+"F2.wireOp",EDGE,"E22.top")])],"isStart":true});
            var Q68;
            Q68=makeQuery(id+"F3.opExtrude","CAP_EDGE",EDGE,{"disambiguationData":[OSD([sQuery(id+"F2.wireOp",EDGE,"E22.bottom")])],"isStart":true});
            var Q69;
            Q69=makeQuery(id+"F3.opExtrude","CAP_EDGE",EDGE,{"disambiguationData":[OSD([sQuery(id+"F2.wireOp",EDGE,"E26")])],"isStart":true});
            var Q70;
            {var subQ0=sQuery(id+"F2.wireOp",EDGE,"E22.bottom");var subQ3=sQuery(id+"F0.wireOp",EDGE,"E10.right");Q70=makeQuery(id+"F3.boolean.opBoolean","SPLIT",EDGE,{"disambiguationData":[TD([makeQuery(id+"F3.opExtrude","SWEPT_FACE",FACE,{"disambiguationData":[OSD([subQ0])]})])],"derivedFrom":makeQuery(id+"F1.opExtrude","CAP_EDGE",EDGE,{"disambiguationData":[OSD([subQ3])],"isStart":false})});}
            var Q71;
            Q71=makeQuery(id+"F1.opExtrude","CAP_EDGE",EDGE,{"disambiguationData":[OSD([sQuery(id+"F0.wireOp",EDGE,"E17.right")])],"isStart":false});
            var Q72;
            {var subQ0=sQuery(id+"F0.wireOp",EDGE,"E20");Q72=makeQuery(id+"F1.opExtrude","CAP_EDGE",EDGE,{"disambiguationData":[OSD([subQ0]),TDD([makeQuery(id+"F0.imprint","IMPRINT",EDGE,{"disambiguationData":[TD([[makeQuery(id+"F0.imprint","INTERSECT",VERTEX,{"derivedFrom":[sQuery(id+"F0.wireOp",EDGE,"E16.left"),subQ0]}),-1.0]])],"derivedFrom":subQ0})])],"isStart":false});}
            var Q73;
            Q73=makeQuery(id+"F1.opExtrude","CAP_EDGE",EDGE,{"disambiguationData":[OSD([sQuery(id+"F0.wireOp",EDGE,"E3.top")])],"isStart":false});
            var Q74;
            Q74=makeQuery(id+"F1.opExtrude","SWEPT_EDGE",EDGE,{"disambiguationData":[OSD([sQuery(id+"F0.wireOp",EDGE,"E3.top"),sQuery(id+"F0.wireOp",EDGE,"E3.right")])]});
            var Q75;
            {var subQ1=sQuery(id+"F0.wireOp",EDGE,"E16.left");var subQ3=sQuery(id+"F2.wireOp",EDGE,"E42.bottom");var subQ4=sQuery(id+"F0.wireOp",EDGE,"E3.right");Q75=makeQuery(id+"F3.boolean.opBoolean","SPLIT",EDGE,{"disambiguationData":[TD([makeQuery(id+"F3.opExtrude","SWEPT_FACE",FACE,{"disambiguationData":[OSD([subQ3])]})])],"derivedFrom":makeQuery(id+"F1.opExtrude","CAP_EDGE",EDGE,{"disambiguationData":[OSD([subQ4,subQ1])],"isStart":false})});}
            var Q76;
            Q76=makeQuery(id+"F3.opExtrude","CAP_EDGE",EDGE,{"disambiguationData":[OSD([sQuery(id+"F2.wireOp",EDGE,"E42.top")])],"isStart":true});
            var Q77;
            Q77=makeQuery(id+"F3.opExtrude","CAP_EDGE",EDGE,{"disambiguationData":[OSD([sQuery(id+"F2.wireOp",EDGE,"E46")])],"isStart":true});
            var Q78;
            Q78=makeQuery(id+"F3.opExtrude","CAP_EDGE",EDGE,{"disambiguationData":[OSD([sQuery(id+"F2.wireOp",EDGE,"E44.filletArc"),sQuery(id+"F2.wireOp",EDGE,"E45.filletArc")])],"isStart":true});
            var Q79;
            Q79=makeQuery(id+"F3.opExtrude","CAP_EDGE",EDGE,{"disambiguationData":[OSD([sQuery(id+"F2.wireOp",EDGE,"E42.bottom")])],"isStart":true});
            var Q80;
            Q80=makeQuery(id+"F1.opExtrude","CAP_EDGE",EDGE,{"disambiguationData":[OSD([sQuery(id+"F0.wireOp",EDGE,"E1.top")])],"isStart":false});
            var Q81;
            Q81=makeQuery(id+"F1.opExtrude","SWEPT_EDGE",EDGE,{"disambiguationData":[OSD([sQuery(id+"F0.wireOp",EDGE,"E19.right"),sQuery(id+"F0.wireOp",EDGE,"E20")])]});
            var Q82;
            Q82=makeQuery(id+"F1.opExtrude","CAP_EDGE",EDGE,{"disambiguationData":[OSD([sQuery(id+"F0.wireOp",EDGE,"E19.right")])],"isStart":true});
            var Q83;
            Q83=makeQuery(id+"F1.opExtrude","SWEPT_EDGE",EDGE,{"disambiguationData":[OSD([sQuery(id+"F0.wireOp",EDGE,"E18.left"),sQuery(id+"F0.wireOp",EDGE,"E20")])]});
            var Q84;
            {var subQ0=sQuery(id+"F0.wireOp",EDGE,"E20");Q84=makeQuery(id+"F1.opExtrude","CAP_EDGE",EDGE,{"disambiguationData":[OSD([subQ0]),TDD([makeQuery(id+"F0.imprint","IMPRINT",EDGE,{"disambiguationData":[TD([[makeQuery(id+"F0.imprint","INTERSECT",VERTEX,{"derivedFrom":[sQuery(id+"F0.wireOp",EDGE,"E18.left"),subQ0]}),-1.0]])],"derivedFrom":subQ0})])],"isStart":true});}
            var Q85;
            Q85=makeQuery(id+"F3.opExtrude","TWEAK_EDGE",EDGE,{"derivedFrom":[makeQuery(id+"F1.opExtrude","CAP_FACE",FACE,{"disambiguationData":[OSD([sQuery(id+"F0.wireOp",EDGE,"E8.top"),sQuery(id+"F0.wireOp",EDGE,"E10.right"),sQuery(id+"F0.wireOp",EDGE,"E13.right"),sQuery(id+"F0.wireOp",EDGE,"E20")])],"isStart":true}),makeQuery(id+"F2.imprint","IMPRINT",EDGE,{"derivedFrom":sQuery(id+"F2.wireOp",EDGE,"E54.filletArc")}),makeQuery(id+"F2.imprint","IMPRINT",EDGE,{"derivedFrom":sQuery(id+"F2.wireOp",EDGE,"E55.filletArc")})]});
            var Q86;
            Q86=makeQuery(id+"F3.opExtrude","TWEAK_EDGE",EDGE,{"derivedFrom":[makeQuery(id+"F1.opExtrude","CAP_FACE",FACE,{"disambiguationData":[OSD([sQuery(id+"F0.wireOp",EDGE,"E8.top"),sQuery(id+"F0.wireOp",EDGE,"E10.right"),sQuery(id+"F0.wireOp",EDGE,"E13.right"),sQuery(id+"F0.wireOp",EDGE,"E20")])],"isStart":true}),makeQuery(id+"F2.imprint","IMPRINT",EDGE,{"derivedFrom":sQuery(id+"F2.wireOp",EDGE,"E52.bottom")})]});
            var Q87;
            Q87=makeQuery(id+"F3.opExtrude","SWEPT_EDGE",EDGE,{"disambiguationData":[OSD([sQuery(id+"F2.wireOp",EDGE,"E52.top"),sQuery(id+"F2.wireOp",EDGE,"E55.filletArc")])]});
            var Q88;
            {var subQ0=sQuery(id+"F0.wireOp",EDGE,"E18.left");var subQ1=sQuery(id+"F0.wireOp",EDGE,"E1.right");Q88=makeQuery(id+"F3.boolean.opBoolean","SPLIT",EDGE,{"disambiguationData":[TD([makeQuery(id+"F3.opExtrude","SWEPT_FACE",FACE,{"disambiguationData":[OSD([sQuery(id+"F2.wireOp",EDGE,"E52.bottom")])]})])],"derivedFrom":makeQuery(id+"F1.opExtrude","CAP_EDGE",EDGE,{"disambiguationData":[OSD([subQ1,subQ0])],"isStart":true})});}
            var Q89;
            Q89=makeQuery(id+"F3.opExtrude","SWEPT_EDGE",EDGE,{"disambiguationData":[OSD([sQuery(id+"F2.wireOp",EDGE,"E52.bottom"),sQuery(id+"F2.wireOp",EDGE,"E52.left")])]});
            var Q90;
            Q90=makeQuery(id+"F3.opExtrude","TWEAK_EDGE",EDGE,{"derivedFrom":[makeQuery(id+"F1.opExtrude","CAP_FACE",FACE,{"disambiguationData":[OSD([sQuery(id+"F0.wireOp",EDGE,"E8.top"),sQuery(id+"F0.wireOp",EDGE,"E10.right"),sQuery(id+"F0.wireOp",EDGE,"E13.right"),sQuery(id+"F0.wireOp",EDGE,"E20")])],"isStart":true}),makeQuery(id+"F2.imprint","IMPRINT",EDGE,{"derivedFrom":sQuery(id+"F2.wireOp",EDGE,"E56")})]});
            var Q91;
            {var subQ0=sQuery(id+"F0.wireOp",EDGE,"E18.left");var subQ1=sQuery(id+"F0.wireOp",EDGE,"E1.right");var subQ3=sQuery(id+"F0.wireOp",EDGE,"E1.top");Q91=makeQuery(id+"F3.boolean.opBoolean","SPLIT",EDGE,{"disambiguationData":[TD([makeQuery(id+"F1.opExtrude","SWEPT_FACE",FACE,{"disambiguationData":[OSD([subQ3])]})])],"derivedFrom":makeQuery(id+"F1.opExtrude","CAP_EDGE",EDGE,{"disambiguationData":[OSD([subQ1,subQ0])],"isStart":true})});}
            var Q92;
            Q92=makeQuery(id+"F3.opExtrude","SWEPT_EDGE",EDGE,{"disambiguationData":[OSD([sQuery(id+"F2.wireOp",EDGE,"E52.top"),sQuery(id+"F2.wireOp",EDGE,"E52.left")])]});
            var Q93;
            Q93=makeQuery(id+"F1.opExtrude","SWEPT_EDGE",EDGE,{"disambiguationData":[OSD([sQuery(id+"F0.wireOp",EDGE,"E5.top"),sQuery(id+"F0.wireOp",EDGE,"E15.bottom"),sQuery(id+"F0.wireOp",EDGE,"E15.right")])]});
            var Q94;
            {var subQ0=sQuery(id+"F0.wireOp",EDGE,"E20");Q94=makeQuery(id+"F1.opExtrude","CAP_EDGE",EDGE,{"disambiguationData":[OSD([subQ0]),TDD([makeQuery(id+"F0.imprint","IMPRINT",EDGE,{"disambiguationData":[TD([[makeQuery(id+"F0.imprint","INTERSECT",VERTEX,{"derivedFrom":[sQuery(id+"F0.wireOp",EDGE,"E14.left"),subQ0]}),-1.0]])],"derivedFrom":subQ0})])],"isStart":true});}
            var Q95;
            Q95=makeQuery(id+"F1.opExtrude","SWEPT_EDGE",EDGE,{"disambiguationData":[OSD([sQuery(id+"F0.wireOp",EDGE,"E14.left"),sQuery(id+"F0.wireOp",EDGE,"E20")])]});
            var Q96;
            Q96=makeQuery(id+"F1.opExtrude","CAP_EDGE",EDGE,{"disambiguationData":[OSD([sQuery(id+"F0.wireOp",EDGE,"E5.top")])],"isStart":true});
            var Q97;
            Q97=makeQuery(id+"F1.opExtrude","CAP_EDGE",EDGE,{"disambiguationData":[OSD([sQuery(id+"F0.wireOp",EDGE,"E15.right")])],"isStart":true});
            var Q98;
            Q98=makeQuery(id+"F1.opExtrude","SWEPT_EDGE",EDGE,{"disambiguationData":[OSD([sQuery(id+"F0.wireOp",EDGE,"E15.right"),sQuery(id+"F0.wireOp",EDGE,"E20")])]});
            var Q99;
            Q99=makeQuery(id+"F3.opExtrude","TWEAK_EDGE",EDGE,{"derivedFrom":[makeQuery(id+"F1.opExtrude","CAP_FACE",FACE,{"disambiguationData":[OSD([sQuery(id+"F0.wireOp",EDGE,"E8.top"),sQuery(id+"F0.wireOp",EDGE,"E10.right"),sQuery(id+"F0.wireOp",EDGE,"E13.right"),sQuery(id+"F0.wireOp",EDGE,"E20")])],"isStart":true}),makeQuery(id+"F2.imprint","IMPRINT",EDGE,{"derivedFrom":sQuery(id+"F2.wireOp",EDGE,"E32.bottom")})]});
            var Q100;
            {var subQ1=sQuery(id+"F0.wireOp",EDGE,"E14.left");var subQ2=sQuery(id+"F0.wireOp",EDGE,"E5.right");var subQ3=sQuery(id+"F0.wireOp",EDGE,"E5.top");Q100=makeQuery(id+"F3.boolean.opBoolean","SPLIT",EDGE,{"disambiguationData":[TD([makeQuery(id+"F1.opExtrude","SWEPT_FACE",FACE,{"disambiguationData":[OSD([subQ3])]})])],"derivedFrom":makeQuery(id+"F1.opExtrude","CAP_EDGE",EDGE,{"disambiguationData":[OSD([subQ2,subQ1])],"isStart":true})});}
            var Q101;
            Q101=makeQuery(id+"F3.opExtrude","SWEPT_EDGE",EDGE,{"disambiguationData":[OSD([sQuery(id+"F2.wireOp",EDGE,"E32.top"),sQuery(id+"F2.wireOp",EDGE,"E32.left")])]});
            var Q102;
            Q102=makeQuery(id+"F3.opExtrude","TWEAK_EDGE",EDGE,{"derivedFrom":[makeQuery(id+"F1.opExtrude","CAP_FACE",FACE,{"disambiguationData":[OSD([sQuery(id+"F0.wireOp",EDGE,"E8.top"),sQuery(id+"F0.wireOp",EDGE,"E10.right"),sQuery(id+"F0.wireOp",EDGE,"E13.right"),sQuery(id+"F0.wireOp",EDGE,"E20")])],"isStart":true}),makeQuery(id+"F2.imprint","IMPRINT",EDGE,{"derivedFrom":sQuery(id+"F2.wireOp",EDGE,"E36")})]});
            var Q103;
            Q103=makeQuery(id+"F3.opExtrude","SWEPT_EDGE",EDGE,{"disambiguationData":[OSD([sQuery(id+"F2.wireOp",EDGE,"E32.bottom"),sQuery(id+"F2.wireOp",EDGE,"E32.left")])]});
            var Q104;
            Q104=makeQuery(id+"F3.opExtrude","TWEAK_EDGE",EDGE,{"derivedFrom":[makeQuery(id+"F1.opExtrude","CAP_FACE",FACE,{"disambiguationData":[OSD([sQuery(id+"F0.wireOp",EDGE,"E8.top"),sQuery(id+"F0.wireOp",EDGE,"E10.right"),sQuery(id+"F0.wireOp",EDGE,"E13.right"),sQuery(id+"F0.wireOp",EDGE,"E20")])],"isStart":true}),makeQuery(id+"F2.imprint","IMPRINT",EDGE,{"derivedFrom":sQuery(id+"F2.wireOp",EDGE,"E34.filletArc")}),makeQuery(id+"F2.imprint","IMPRINT",EDGE,{"derivedFrom":sQuery(id+"F2.wireOp",EDGE,"E35.filletArc")})]});
            var Q105;
            {var subQ1=sQuery(id+"F0.wireOp",EDGE,"E14.left");var subQ3=sQuery(id+"F0.wireOp",EDGE,"E5.right");Q105=makeQuery(id+"F3.boolean.opBoolean","SPLIT",EDGE,{"disambiguationData":[TD([makeQuery(id+"F3.opExtrude","SWEPT_FACE",FACE,{"disambiguationData":[OSD([sQuery(id+"F2.wireOp",EDGE,"E32.bottom")])]})])],"derivedFrom":makeQuery(id+"F1.opExtrude","CAP_EDGE",EDGE,{"disambiguationData":[OSD([subQ3,subQ1])],"isStart":true})});}
            var Q106;
            Q106=makeQuery(id+"F1.opExtrude","CAP_EDGE",EDGE,{"disambiguationData":[OSD([sQuery(id+"F0.wireOp",EDGE,"E2.top")])],"isStart":true});
            var Q107;
            {var subQ0=sQuery(id+"F0.wireOp",EDGE,"E20");Q107=makeQuery(id+"F1.opExtrude","CAP_EDGE",EDGE,{"disambiguationData":[OSD([subQ0]),TDD([makeQuery(id+"F0.imprint","IMPRINT",EDGE,{"disambiguationData":[TD([[makeQuery(id+"F0.imprint","INTERSECT",VERTEX,{"derivedFrom":[sQuery(id+"F0.wireOp",EDGE,"E17.left"),subQ0]}),-1.0]])],"derivedFrom":subQ0})])],"isStart":true});}
            var Q108;
            Q108=makeQuery(id+"F1.opExtrude","SWEPT_EDGE",EDGE,{"disambiguationData":[OSD([sQuery(id+"F0.wireOp",EDGE,"E17.left"),sQuery(id+"F0.wireOp",EDGE,"E20")])]});
            var Q109;
            Q109=makeQuery(id+"F1.opExtrude","CAP_EDGE",EDGE,{"disambiguationData":[OSD([sQuery(id+"F0.wireOp",EDGE,"E18.right")])],"isStart":true});
            var Q110;
            Q110=makeQuery(id+"F1.opExtrude","SWEPT_EDGE",EDGE,{"disambiguationData":[OSD([sQuery(id+"F0.wireOp",EDGE,"E18.right"),sQuery(id+"F0.wireOp",EDGE,"E20")])]});
            var Q111;
            Q111=makeQuery(id+"F1.opExtrude","SWEPT_EDGE",EDGE,{"disambiguationData":[OSD([sQuery(id+"F0.wireOp",EDGE,"E2.top"),sQuery(id+"F0.wireOp",EDGE,"E18.bottom"),sQuery(id+"F0.wireOp",EDGE,"E18.right")])]});
            var Q112;
            {var subQ0=sQuery(id+"F0.wireOp",EDGE,"E17.left");var subQ1=sQuery(id+"F0.wireOp",EDGE,"E2.right");var subQ3=sQuery(id+"F0.wireOp",EDGE,"E2.top");Q112=makeQuery(id+"F3.boolean.opBoolean","SPLIT",EDGE,{"disambiguationData":[TD([makeQuery(id+"F1.opExtrude","SWEPT_FACE",FACE,{"disambiguationData":[OSD([subQ3])]})])],"derivedFrom":makeQuery(id+"F1.opExtrude","CAP_EDGE",EDGE,{"disambiguationData":[OSD([subQ1,subQ0])],"isStart":true})});}
            var Q113;
            {var subQ0=sQuery(id+"F0.wireOp",EDGE,"E17.left");var subQ1=sQuery(id+"F0.wireOp",EDGE,"E2.right");Q113=makeQuery(id+"F3.boolean.opBoolean","SPLIT",EDGE,{"disambiguationData":[TD([makeQuery(id+"F3.opExtrude","SWEPT_FACE",FACE,{"disambiguationData":[OSD([sQuery(id+"F2.wireOp",EDGE,"E47.bottom")])]})])],"derivedFrom":makeQuery(id+"F1.opExtrude","CAP_EDGE",EDGE,{"disambiguationData":[OSD([subQ1,subQ0])],"isStart":true})});}
            var Q114;
            Q114=makeQuery(id+"F3.opExtrude","SWEPT_EDGE",EDGE,{"disambiguationData":[OSD([sQuery(id+"F2.wireOp",EDGE,"E47.top"),sQuery(id+"F2.wireOp",EDGE,"E47.left")])]});
            var Q115;
            Q115=makeQuery(id+"F3.opExtrude","SWEPT_EDGE",EDGE,{"disambiguationData":[OSD([sQuery(id+"F2.wireOp",EDGE,"E47.bottom"),sQuery(id+"F2.wireOp",EDGE,"E47.left")])]});
            var Q116;
            Q116=makeQuery(id+"F3.opExtrude","SWEPT_EDGE",EDGE,{"disambiguationData":[OSD([sQuery(id+"F2.wireOp",EDGE,"E47.top"),sQuery(id+"F2.wireOp",EDGE,"E50.filletArc")])]});
            var Q117;
            Q117=makeQuery(id+"F3.opExtrude","TWEAK_EDGE",EDGE,{"derivedFrom":[makeQuery(id+"F1.opExtrude","CAP_FACE",FACE,{"disambiguationData":[OSD([sQuery(id+"F0.wireOp",EDGE,"E8.top"),sQuery(id+"F0.wireOp",EDGE,"E10.right"),sQuery(id+"F0.wireOp",EDGE,"E13.right"),sQuery(id+"F0.wireOp",EDGE,"E20")])],"isStart":true}),makeQuery(id+"F2.imprint","IMPRINT",EDGE,{"derivedFrom":sQuery(id+"F2.wireOp",EDGE,"E47.bottom")})]});
            var Q118;
            Q118=makeQuery(id+"F3.opExtrude","SWEPT_EDGE",EDGE,{"disambiguationData":[OSD([sQuery(id+"F2.wireOp",EDGE,"E47.bottom"),sQuery(id+"F2.wireOp",EDGE,"E49.filletArc")])]});
            var Q119;
            Q119=makeQuery(id+"F3.opExtrude","TWEAK_EDGE",EDGE,{"derivedFrom":[makeQuery(id+"F1.opExtrude","CAP_FACE",FACE,{"disambiguationData":[OSD([sQuery(id+"F0.wireOp",EDGE,"E8.top"),sQuery(id+"F0.wireOp",EDGE,"E10.right"),sQuery(id+"F0.wireOp",EDGE,"E13.right"),sQuery(id+"F0.wireOp",EDGE,"E20")])],"isStart":true}),makeQuery(id+"F2.imprint","IMPRINT",EDGE,{"derivedFrom":sQuery(id+"F2.wireOp",EDGE,"E51")})]});
            var Q120;
            Q120=makeQuery(id+"F1.opExtrude","SWEPT_EDGE",EDGE,{"disambiguationData":[OSD([sQuery(id+"F0.wireOp",EDGE,"E20"),sQuery(id+"F0.wireOp",EDGE,"E21.top"),sQuery(id+"F0.wireOp",EDGE,"E21.right")])]});
            var Q121;
            Q121=makeQuery(id+"F3.opExtrude","SWEPT_EDGE",EDGE,{"disambiguationData":[OSD([sQuery(id+"F2.wireOp",EDGE,"E57.bottom"),sQuery(id+"F2.wireOp",EDGE,"E57.left")])]});
            var Q122;
            Q122=makeQuery(id+"F1.opExtrude","CAP_EDGE",EDGE,{"disambiguationData":[OSD([sQuery(id+"F0.wireOp",EDGE,"E0.top")])],"isStart":false});
            var Q123;
            Q123=makeQuery(id+"F3.opExtrude","SWEPT_EDGE",EDGE,{"disambiguationData":[OSD([sQuery(id+"F2.wireOp",EDGE,"E57.top"),sQuery(id+"F2.wireOp",EDGE,"E57.left")])]});
            var Q124;
            Q124=makeQuery(id+"F1.opExtrude","SWEPT_EDGE",EDGE,{"disambiguationData":[OSD([sQuery(id+"F0.wireOp",EDGE,"E19.left"),sQuery(id+"F0.wireOp",EDGE,"E20")])]});
            var Q125;
            Q125=makeQuery(id+"F1.opExtrude","CAP_EDGE",EDGE,{"disambiguationData":[OSD([sQuery(id+"F0.wireOp",EDGE,"E21.right")])],"isStart":true});
            var Q126;
            {var subQ0=sQuery(id+"F0.wireOp",EDGE,"E20");Q126=makeQuery(id+"F1.opExtrude","CAP_EDGE",EDGE,{"disambiguationData":[OSD([subQ0]),TDD([makeQuery(id+"F0.imprint","IMPRINT",EDGE,{"disambiguationData":[TD([[makeQuery(id+"F0.imprint","INTERSECT",VERTEX,{"derivedFrom":[sQuery(id+"F0.wireOp",EDGE,"E19.left"),subQ0]}),-1.0]])],"derivedFrom":subQ0})])],"isStart":true});}
            var Q127;
            Q127=makeQuery(id+"F3.opExtrude","TWEAK_EDGE",EDGE,{"derivedFrom":[makeQuery(id+"F1.opExtrude","CAP_FACE",FACE,{"disambiguationData":[OSD([sQuery(id+"F0.wireOp",EDGE,"E8.top"),sQuery(id+"F0.wireOp",EDGE,"E10.right"),sQuery(id+"F0.wireOp",EDGE,"E13.right"),sQuery(id+"F0.wireOp",EDGE,"E20")])],"isStart":true}),makeQuery(id+"F2.imprint","IMPRINT",EDGE,{"derivedFrom":sQuery(id+"F2.wireOp",EDGE,"E59.filletArc")}),makeQuery(id+"F2.imprint","IMPRINT",EDGE,{"derivedFrom":sQuery(id+"F2.wireOp",EDGE,"E60.filletArc")})]});
            var Q128;
            Q128=makeQuery(id+"F3.opExtrude","TWEAK_EDGE",EDGE,{"derivedFrom":[makeQuery(id+"F1.opExtrude","CAP_FACE",FACE,{"disambiguationData":[OSD([sQuery(id+"F0.wireOp",EDGE,"E8.top"),sQuery(id+"F0.wireOp",EDGE,"E10.right"),sQuery(id+"F0.wireOp",EDGE,"E13.right"),sQuery(id+"F0.wireOp",EDGE,"E20")])],"isStart":true}),makeQuery(id+"F2.imprint","IMPRINT",EDGE,{"derivedFrom":sQuery(id+"F2.wireOp",EDGE,"E57.bottom")})]});
            var Q129;
            Q129=makeQuery(id+"F3.opExtrude","TWEAK_EDGE",EDGE,{"derivedFrom":[makeQuery(id+"F1.opExtrude","CAP_FACE",FACE,{"disambiguationData":[OSD([sQuery(id+"F0.wireOp",EDGE,"E8.top"),sQuery(id+"F0.wireOp",EDGE,"E10.right"),sQuery(id+"F0.wireOp",EDGE,"E13.right"),sQuery(id+"F0.wireOp",EDGE,"E20")])],"isStart":true}),makeQuery(id+"F2.imprint","IMPRINT",EDGE,{"derivedFrom":sQuery(id+"F2.wireOp",EDGE,"E61")})]});
            var Q130;
            {var subQ1=sQuery(id+"F0.wireOp",EDGE,"E19.left");var subQ2=sQuery(id+"F0.wireOp",EDGE,"E0.right");var subQ3=sQuery(id+"F0.wireOp",EDGE,"E0.top");Q130=makeQuery(id+"F3.boolean.opBoolean","SPLIT",EDGE,{"disambiguationData":[TD([makeQuery(id+"F1.opExtrude","SWEPT_FACE",FACE,{"disambiguationData":[OSD([subQ3])]})])],"derivedFrom":makeQuery(id+"F1.opExtrude","CAP_EDGE",EDGE,{"disambiguationData":[OSD([subQ2,subQ1])],"isStart":true})});}
            var Q131;
            {var subQ0=sQuery(id+"F0.wireOp",EDGE,"E19.left");var subQ1=sQuery(id+"F0.wireOp",EDGE,"E0.right");Q131=makeQuery(id+"F3.boolean.opBoolean","SPLIT",EDGE,{"disambiguationData":[TD([makeQuery(id+"F3.opExtrude","SWEPT_FACE",FACE,{"disambiguationData":[OSD([sQuery(id+"F2.wireOp",EDGE,"E57.bottom")])]})])],"derivedFrom":makeQuery(id+"F1.opExtrude","CAP_EDGE",EDGE,{"disambiguationData":[OSD([subQ1,subQ0])],"isStart":true})});}
            var Q132;
            Q132=makeQuery(id+"F3.opExtrude","SWEPT_EDGE",EDGE,{"disambiguationData":[OSD([sQuery(id+"F2.wireOp",EDGE,"E57.bottom"),sQuery(id+"F2.wireOp",EDGE,"E59.filletArc")])]});
            var Q133;
            Q133=makeQuery(id+"F3.opExtrude","SWEPT_EDGE",EDGE,{"disambiguationData":[OSD([sQuery(id+"F2.wireOp",EDGE,"E27.top"),sQuery(id+"F2.wireOp",EDGE,"E27.left")])]});
            var Q134;
            Q134=makeQuery(id+"F3.opExtrude","TWEAK_EDGE",EDGE,{"derivedFrom":[makeQuery(id+"F1.opExtrude","CAP_FACE",FACE,{"disambiguationData":[OSD([sQuery(id+"F0.wireOp",EDGE,"E8.top"),sQuery(id+"F0.wireOp",EDGE,"E10.right"),sQuery(id+"F0.wireOp",EDGE,"E13.right"),sQuery(id+"F0.wireOp",EDGE,"E20")])],"isStart":true}),makeQuery(id+"F2.imprint","IMPRINT",EDGE,{"derivedFrom":sQuery(id+"F2.wireOp",EDGE,"E31")})]});
            var Q135;
            Q135=makeQuery(id+"F3.opExtrude","TWEAK_EDGE",EDGE,{"derivedFrom":[makeQuery(id+"F1.opExtrude","CAP_FACE",FACE,{"disambiguationData":[OSD([sQuery(id+"F0.wireOp",EDGE,"E8.top"),sQuery(id+"F0.wireOp",EDGE,"E10.right"),sQuery(id+"F0.wireOp",EDGE,"E13.right"),sQuery(id+"F0.wireOp",EDGE,"E20")])],"isStart":true}),makeQuery(id+"F2.imprint","IMPRINT",EDGE,{"derivedFrom":sQuery(id+"F2.wireOp",EDGE,"E27.bottom")})]});
            var Q136;
            {var subQ1=sQuery(id+"F0.wireOp",EDGE,"E13.left");var subQ3=sQuery(id+"F0.wireOp",EDGE,"E8.left");Q136=makeQuery(id+"F3.boolean.opBoolean","SPLIT",EDGE,{"disambiguationData":[TD([makeQuery(id+"F3.opExtrude","SWEPT_FACE",FACE,{"disambiguationData":[OSD([sQuery(id+"F2.wireOp",EDGE,"E27.bottom")])]})])],"derivedFrom":makeQuery(id+"F1.opExtrude","CAP_EDGE",EDGE,{"disambiguationData":[OSD([subQ3,subQ1])],"isStart":true})});}
            var Q137;
            {var subQ0=sQuery(id+"F0.wireOp",EDGE,"E20");Q137=makeQuery(id+"F1.opExtrude","CAP_EDGE",EDGE,{"disambiguationData":[OSD([subQ0]),TDD([makeQuery(id+"F0.imprint","IMPRINT",EDGE,{"disambiguationData":[TD([[makeQuery(id+"F0.imprint","INTERSECT",VERTEX,{"derivedFrom":[sQuery(id+"F0.wireOp",EDGE,"E13.left"),subQ0]}),-1.0]])],"derivedFrom":subQ0})])],"isStart":true});}
            var Q138;
            Q138=makeQuery(id+"F1.opExtrude","SWEPT_EDGE",EDGE,{"disambiguationData":[OSD([sQuery(id+"F0.wireOp",EDGE,"E13.left"),sQuery(id+"F0.wireOp",EDGE,"E20")])]});
            var Q139;
            Q139=makeQuery(id+"F1.opExtrude","CAP_EDGE",EDGE,{"disambiguationData":[OSD([sQuery(id+"F0.wireOp",EDGE,"E14.right")])],"isStart":true});
            var Q140;
            Q140=makeQuery(id+"F1.opExtrude","SWEPT_EDGE",EDGE,{"disambiguationData":[OSD([sQuery(id+"F0.wireOp",EDGE,"E14.right"),sQuery(id+"F0.wireOp",EDGE,"E20")])]});
            var Q141;
            Q141=makeQuery(id+"F1.opExtrude","CAP_EDGE",EDGE,{"disambiguationData":[OSD([sQuery(id+"F0.wireOp",EDGE,"E6")])],"isStart":false});
            var Q142;
            {var subQ0=sQuery(id+"F0.wireOp",EDGE,"E13.left");var subQ1=sQuery(id+"F0.wireOp",EDGE,"E8.left");var subQ3=sQuery(id+"F0.wireOp",EDGE,"E6");Q142=makeQuery(id+"F3.boolean.opBoolean","SPLIT",EDGE,{"disambiguationData":[TD([makeQuery(id+"F1.opExtrude","SWEPT_FACE",FACE,{"disambiguationData":[OSD([subQ3])]})])],"derivedFrom":makeQuery(id+"F1.opExtrude","CAP_EDGE",EDGE,{"disambiguationData":[OSD([subQ1,subQ0])],"isStart":true})});}
            var Q143;
            Q143=makeQuery(id+"F3.opExtrude","SWEPT_EDGE",EDGE,{"disambiguationData":[OSD([sQuery(id+"F2.wireOp",EDGE,"E27.top"),sQuery(id+"F2.wireOp",EDGE,"E30.filletArc")])]});
            var Q144;
            Q144=makeQuery(id+"F3.opExtrude","SWEPT_EDGE",EDGE,{"disambiguationData":[OSD([sQuery(id+"F2.wireOp",EDGE,"E27.bottom"),sQuery(id+"F2.wireOp",EDGE,"E27.left")])]});
            var Q145;
            Q145=makeQuery(id+"F3.opExtrude","SWEPT_EDGE",EDGE,{"disambiguationData":[OSD([sQuery(id+"F2.wireOp",EDGE,"E27.bottom"),sQuery(id+"F2.wireOp",EDGE,"E29.filletArc")])]});
            var Q146;
            {var subQ0=sQuery(id+"F0.wireOp",EDGE,"E20");Q146=makeQuery(id+"F1.opExtrude","CAP_EDGE",EDGE,{"disambiguationData":[OSD([subQ0]),TDD([makeQuery(id+"F0.imprint","IMPRINT",EDGE,{"disambiguationData":[TD([[makeQuery(id+"F0.imprint","INTERSECT",VERTEX,{"derivedFrom":[sQuery(id+"F0.wireOp",EDGE,"E15.left"),subQ0]}),-1.0]])],"derivedFrom":subQ0})])],"isStart":true});}
            var Q147;
            Q147=makeQuery(id+"F1.opExtrude","SWEPT_EDGE",EDGE,{"disambiguationData":[OSD([sQuery(id+"F0.wireOp",EDGE,"E15.left"),sQuery(id+"F0.wireOp",EDGE,"E20")])]});
            var Q148;
            Q148=makeQuery(id+"F1.opExtrude","CAP_EDGE",EDGE,{"disambiguationData":[OSD([sQuery(id+"F0.wireOp",EDGE,"E16.right")])],"isStart":true});
            var Q149;
            Q149=makeQuery(id+"F1.opExtrude","SWEPT_EDGE",EDGE,{"disambiguationData":[OSD([sQuery(id+"F0.wireOp",EDGE,"E16.right"),sQuery(id+"F0.wireOp",EDGE,"E20")])]});
            var Q150;
            Q150=makeQuery(id+"F1.opExtrude","CAP_EDGE",EDGE,{"disambiguationData":[OSD([sQuery(id+"F0.wireOp",EDGE,"E4.top")])],"isStart":true});
            var Q151;
            Q151=makeQuery(id+"F1.opExtrude","SWEPT_EDGE",EDGE,{"disambiguationData":[OSD([sQuery(id+"F0.wireOp",EDGE,"E4.top"),sQuery(id+"F0.wireOp",EDGE,"E16.bottom"),sQuery(id+"F0.wireOp",EDGE,"E16.right")])]});
            var Q152;
            Q152=makeQuery(id+"F3.opExtrude","SWEPT_EDGE",EDGE,{"disambiguationData":[OSD([sQuery(id+"F2.wireOp",EDGE,"E37.bottom"),sQuery(id+"F2.wireOp",EDGE,"E37.left")])]});
            var Q153;
            Q153=makeQuery(id+"F3.opExtrude","TWEAK_EDGE",EDGE,{"derivedFrom":[makeQuery(id+"F1.opExtrude","CAP_FACE",FACE,{"disambiguationData":[OSD([sQuery(id+"F0.wireOp",EDGE,"E8.top"),sQuery(id+"F0.wireOp",EDGE,"E10.right"),sQuery(id+"F0.wireOp",EDGE,"E13.right"),sQuery(id+"F0.wireOp",EDGE,"E20")])],"isStart":true}),makeQuery(id+"F2.imprint","IMPRINT",EDGE,{"derivedFrom":sQuery(id+"F2.wireOp",EDGE,"E37.bottom")})]});
            var Q154;
            {var subQ1=sQuery(id+"F0.wireOp",EDGE,"E15.left");var subQ2=sQuery(id+"F0.wireOp",EDGE,"E4.right");Q154=makeQuery(id+"F3.boolean.opBoolean","SPLIT",EDGE,{"disambiguationData":[TD([makeQuery(id+"F3.opExtrude","SWEPT_FACE",FACE,{"disambiguationData":[OSD([sQuery(id+"F2.wireOp",EDGE,"E37.bottom")])]})])],"derivedFrom":makeQuery(id+"F1.opExtrude","CAP_EDGE",EDGE,{"disambiguationData":[OSD([subQ2,subQ1])],"isStart":true})});}
            var Q155;
            Q155=makeQuery(id+"F3.opExtrude","TWEAK_EDGE",EDGE,{"derivedFrom":[makeQuery(id+"F1.opExtrude","CAP_FACE",FACE,{"disambiguationData":[OSD([sQuery(id+"F0.wireOp",EDGE,"E8.top"),sQuery(id+"F0.wireOp",EDGE,"E10.right"),sQuery(id+"F0.wireOp",EDGE,"E13.right"),sQuery(id+"F0.wireOp",EDGE,"E20")])],"isStart":true}),makeQuery(id+"F2.imprint","IMPRINT",EDGE,{"derivedFrom":sQuery(id+"F2.wireOp",EDGE,"E39.filletArc")}),makeQuery(id+"F2.imprint","IMPRINT",EDGE,{"derivedFrom":sQuery(id+"F2.wireOp",EDGE,"E40.filletArc")})]});
            var Q156;
            Q156=makeQuery(id+"F3.opExtrude","TWEAK_EDGE",EDGE,{"derivedFrom":[makeQuery(id+"F1.opExtrude","CAP_FACE",FACE,{"disambiguationData":[OSD([sQuery(id+"F0.wireOp",EDGE,"E8.top"),sQuery(id+"F0.wireOp",EDGE,"E10.right"),sQuery(id+"F0.wireOp",EDGE,"E13.right"),sQuery(id+"F0.wireOp",EDGE,"E20")])],"isStart":true}),makeQuery(id+"F2.imprint","IMPRINT",EDGE,{"derivedFrom":sQuery(id+"F2.wireOp",EDGE,"E41")})]});
            var Q157;
            Q157=makeQuery(id+"F3.opExtrude","SWEPT_EDGE",EDGE,{"disambiguationData":[OSD([sQuery(id+"F2.wireOp",EDGE,"E37.top"),sQuery(id+"F2.wireOp",EDGE,"E40.filletArc")])]});
            var Q158;
            Q158=makeQuery(id+"F3.opExtrude","SWEPT_EDGE",EDGE,{"disambiguationData":[OSD([sQuery(id+"F2.wireOp",EDGE,"E37.top"),sQuery(id+"F2.wireOp",EDGE,"E37.left")])]});
            var Q159;
            {var subQ0=sQuery(id+"F0.wireOp",EDGE,"E4.top");var subQ1=sQuery(id+"F0.wireOp",EDGE,"E15.left");var subQ2=sQuery(id+"F0.wireOp",EDGE,"E4.right");Q159=makeQuery(id+"F3.boolean.opBoolean","SPLIT",EDGE,{"disambiguationData":[TD([makeQuery(id+"F1.opExtrude","SWEPT_FACE",FACE,{"disambiguationData":[OSD([subQ0])]})])],"derivedFrom":makeQuery(id+"F1.opExtrude","CAP_EDGE",EDGE,{"disambiguationData":[OSD([subQ2,subQ1])],"isStart":true})});}
            var Q160;
            Q160=makeQuery(id+"F1.opExtrude","SWEPT_EDGE",EDGE,{"disambiguationData":[OSD([sQuery(id+"F0.wireOp",EDGE,"E13.right"),sQuery(id+"F0.wireOp",EDGE,"E20")])]});
            var Q161;
            {var subQ0=sQuery(id+"F0.wireOp",EDGE,"E20");Q161=makeQuery(id+"F1.opExtrude","CAP_EDGE",EDGE,{"disambiguationData":[OSD([subQ0]),TDD([makeQuery(id+"F0.imprint","IMPRINT",EDGE,{"disambiguationData":[TD([[makeQuery(id+"F0.imprint","INTERSECT",VERTEX,{"derivedFrom":[sQuery(id+"F0.wireOp",EDGE,"E10.right"),subQ0]}),-1.0]])],"derivedFrom":subQ0})])],"isStart":true});}
            var Q162;
            Q162=makeQuery(id+"F1.opExtrude","CAP_EDGE",EDGE,{"disambiguationData":[OSD([sQuery(id+"F0.wireOp",EDGE,"E8.top")])],"isStart":false});
            var Q163;
            Q163=makeQuery(id+"F1.opExtrude","SWEPT_EDGE",EDGE,{"disambiguationData":[OSD([sQuery(id+"F0.wireOp",EDGE,"E8.top"),sQuery(id+"F0.wireOp",EDGE,"E10.right")])]});
            var Q164;
            Q164=makeQuery(id+"F1.opExtrude","CAP_EDGE",EDGE,{"disambiguationData":[OSD([sQuery(id+"F0.wireOp",EDGE,"E13.right")])],"isStart":true});
            var Q165;
            Q165=makeQuery(id+"F1.opExtrude","SWEPT_EDGE",EDGE,{"disambiguationData":[OSD([sQuery(id+"F0.wireOp",EDGE,"E10.right"),sQuery(id+"F0.wireOp",EDGE,"E20")])]});
            var Q166;
            Q166=makeQuery(id+"F3.opExtrude","SWEPT_EDGE",EDGE,{"disambiguationData":[OSD([sQuery(id+"F0.wireOp",EDGE,"E10.right"),sQuery(id+"F2.wireOp",EDGE,"E22.top"),sQuery(id+"F2.wireOp",EDGE,"E22.left")])]});
            var Q167;
            Q167=makeQuery(id+"F3.opExtrude","SWEPT_EDGE",EDGE,{"disambiguationData":[OSD([sQuery(id+"F0.wireOp",EDGE,"E10.right"),sQuery(id+"F2.wireOp",EDGE,"E22.bottom"),sQuery(id+"F2.wireOp",EDGE,"E22.left")])]});
            var Q168;
            Q168=makeQuery(id+"F3.opExtrude","TWEAK_EDGE",EDGE,{"derivedFrom":[makeQuery(id+"F1.opExtrude","CAP_FACE",FACE,{"disambiguationData":[OSD([sQuery(id+"F0.wireOp",EDGE,"E8.top"),sQuery(id+"F0.wireOp",EDGE,"E10.right"),sQuery(id+"F0.wireOp",EDGE,"E13.right"),sQuery(id+"F0.wireOp",EDGE,"E20")])],"isStart":true}),makeQuery(id+"F2.imprint","IMPRINT",EDGE,{"derivedFrom":sQuery(id+"F2.wireOp",EDGE,"E24.filletArc")}),makeQuery(id+"F2.imprint","IMPRINT",EDGE,{"derivedFrom":sQuery(id+"F2.wireOp",EDGE,"E25.filletArc")})]});
            var Q169;
            Q169=makeQuery(id+"F3.opExtrude","TWEAK_EDGE",EDGE,{"derivedFrom":[makeQuery(id+"F1.opExtrude","CAP_FACE",FACE,{"disambiguationData":[OSD([sQuery(id+"F0.wireOp",EDGE,"E8.top"),sQuery(id+"F0.wireOp",EDGE,"E10.right"),sQuery(id+"F0.wireOp",EDGE,"E13.right"),sQuery(id+"F0.wireOp",EDGE,"E20")])],"isStart":true}),makeQuery(id+"F2.imprint","IMPRINT",EDGE,{"derivedFrom":sQuery(id+"F2.wireOp",EDGE,"E26")})]});
            var Q170;
            Q170=makeQuery(id+"F3.opExtrude","SWEPT_EDGE",EDGE,{"disambiguationData":[OSD([sQuery(id+"F2.wireOp",EDGE,"E22.bottom"),sQuery(id+"F2.wireOp",EDGE,"E24.filletArc")])]});
            var Q171;
            Q171=makeQuery(id+"F3.opExtrude","TWEAK_EDGE",EDGE,{"derivedFrom":[makeQuery(id+"F1.opExtrude","CAP_FACE",FACE,{"disambiguationData":[OSD([sQuery(id+"F0.wireOp",EDGE,"E8.top"),sQuery(id+"F0.wireOp",EDGE,"E10.right"),sQuery(id+"F0.wireOp",EDGE,"E13.right"),sQuery(id+"F0.wireOp",EDGE,"E20")])],"isStart":true}),makeQuery(id+"F2.imprint","IMPRINT",EDGE,{"derivedFrom":sQuery(id+"F2.wireOp",EDGE,"E22.bottom")})]});
            var Q172;
            Q172=makeQuery(id+"F3.opExtrude","SWEPT_EDGE",EDGE,{"disambiguationData":[OSD([sQuery(id+"F2.wireOp",EDGE,"E22.top"),sQuery(id+"F2.wireOp",EDGE,"E25.filletArc")])]});
            var Q173;
            {var subQ1=sQuery(id+"F0.wireOp",EDGE,"E10.right");Q173=makeQuery(id+"F3.boolean.opBoolean","SPLIT",EDGE,{"disambiguationData":[TD([makeQuery(id+"F3.opExtrude","SWEPT_FACE",FACE,{"disambiguationData":[OSD([sQuery(id+"F2.wireOp",EDGE,"E22.bottom")])]})])],"derivedFrom":makeQuery(id+"F1.opExtrude","CAP_EDGE",EDGE,{"disambiguationData":[OSD([subQ1])],"isStart":true})});}
            var Q174;
            Q174=makeQuery(id+"F1.opExtrude","CAP_EDGE",EDGE,{"disambiguationData":[OSD([sQuery(id+"F0.wireOp",EDGE,"E3.top")])],"isStart":true});
            var Q175;
            Q175=makeQuery(id+"F1.opExtrude","SWEPT_EDGE",EDGE,{"disambiguationData":[OSD([sQuery(id+"F0.wireOp",EDGE,"E17.right"),sQuery(id+"F0.wireOp",EDGE,"E20")])]});
            var Q176;
            Q176=makeQuery(id+"F1.opExtrude","CAP_EDGE",EDGE,{"disambiguationData":[OSD([sQuery(id+"F0.wireOp",EDGE,"E17.right")])],"isStart":true});
            var Q177;
            Q177=makeQuery(id+"F1.opExtrude","SWEPT_EDGE",EDGE,{"disambiguationData":[OSD([sQuery(id+"F0.wireOp",EDGE,"E16.left"),sQuery(id+"F0.wireOp",EDGE,"E20")])]});
            var Q178;
            {var subQ0=sQuery(id+"F0.wireOp",EDGE,"E20");Q178=makeQuery(id+"F1.opExtrude","CAP_EDGE",EDGE,{"disambiguationData":[OSD([subQ0]),TDD([makeQuery(id+"F0.imprint","IMPRINT",EDGE,{"disambiguationData":[TD([[makeQuery(id+"F0.imprint","INTERSECT",VERTEX,{"derivedFrom":[sQuery(id+"F0.wireOp",EDGE,"E16.left"),subQ0]}),-1.0]])],"derivedFrom":subQ0})])],"isStart":true});}
            var Q179;
            Q179=makeQuery(id+"F1.opExtrude","SWEPT_EDGE",EDGE,{"disambiguationData":[OSD([sQuery(id+"F0.wireOp",EDGE,"E3.top"),sQuery(id+"F0.wireOp",EDGE,"E17.bottom"),sQuery(id+"F0.wireOp",EDGE,"E17.right")])]});
            var Q180;
            Q180=makeQuery(id+"F3.opExtrude","TWEAK_EDGE",EDGE,{"derivedFrom":[makeQuery(id+"F1.opExtrude","CAP_FACE",FACE,{"disambiguationData":[OSD([sQuery(id+"F0.wireOp",EDGE,"E8.top"),sQuery(id+"F0.wireOp",EDGE,"E10.right"),sQuery(id+"F0.wireOp",EDGE,"E13.right"),sQuery(id+"F0.wireOp",EDGE,"E20")])],"isStart":true}),makeQuery(id+"F2.imprint","IMPRINT",EDGE,{"derivedFrom":sQuery(id+"F2.wireOp",EDGE,"E46")})]});
            var Q181;
            Q181=makeQuery(id+"F3.opExtrude","TWEAK_EDGE",EDGE,{"derivedFrom":[makeQuery(id+"F1.opExtrude","CAP_FACE",FACE,{"disambiguationData":[OSD([sQuery(id+"F0.wireOp",EDGE,"E8.top"),sQuery(id+"F0.wireOp",EDGE,"E10.right"),sQuery(id+"F0.wireOp",EDGE,"E13.right"),sQuery(id+"F0.wireOp",EDGE,"E20")])],"isStart":true}),makeQuery(id+"F2.imprint","IMPRINT",EDGE,{"derivedFrom":sQuery(id+"F2.wireOp",EDGE,"E42.bottom")})]});
            var Q182;
            Q182=makeQuery(id+"F3.opExtrude","SWEPT_EDGE",EDGE,{"disambiguationData":[OSD([sQuery(id+"F2.wireOp",EDGE,"E42.top"),sQuery(id+"F2.wireOp",EDGE,"E45.filletArc")])]});
            var Q183;
            Q183=makeQuery(id+"F3.opExtrude","SWEPT_EDGE",EDGE,{"disambiguationData":[OSD([sQuery(id+"F2.wireOp",EDGE,"E42.top"),sQuery(id+"F2.wireOp",EDGE,"E42.left")])]});
            var Q184;
            {var subQ0=sQuery(id+"F0.wireOp",EDGE,"E16.left");var subQ1=sQuery(id+"F0.wireOp",EDGE,"E3.right");Q184=makeQuery(id+"F3.boolean.opBoolean","SPLIT",EDGE,{"disambiguationData":[TD([makeQuery(id+"F3.opExtrude","SWEPT_FACE",FACE,{"disambiguationData":[OSD([sQuery(id+"F2.wireOp",EDGE,"E42.bottom")])]})])],"derivedFrom":makeQuery(id+"F1.opExtrude","CAP_EDGE",EDGE,{"disambiguationData":[OSD([subQ1,subQ0])],"isStart":true})});}
            var Q185;
            {var subQ0=sQuery(id+"F0.wireOp",EDGE,"E16.left");var subQ1=sQuery(id+"F0.wireOp",EDGE,"E3.right");var subQ3=sQuery(id+"F0.wireOp",EDGE,"E3.top");Q185=makeQuery(id+"F3.boolean.opBoolean","SPLIT",EDGE,{"disambiguationData":[TD([makeQuery(id+"F1.opExtrude","SWEPT_FACE",FACE,{"disambiguationData":[OSD([subQ3])]})])],"derivedFrom":makeQuery(id+"F1.opExtrude","CAP_EDGE",EDGE,{"disambiguationData":[OSD([subQ1,subQ0])],"isStart":true})});}
            var Q186;
            Q186=makeQuery(id+"F3.opExtrude","SWEPT_EDGE",EDGE,{"disambiguationData":[OSD([sQuery(id+"F2.wireOp",EDGE,"E42.bottom"),sQuery(id+"F2.wireOp",EDGE,"E42.left")])]});
            var Q187;
            Q187=makeQuery(id+"F3.opExtrude","SWEPT_EDGE",EDGE,{"disambiguationData":[OSD([sQuery(id+"F2.wireOp",EDGE,"E42.bottom"),sQuery(id+"F2.wireOp",EDGE,"E44.filletArc")])]});
            var Q188;
            Q188=makeQuery(id+"F1.opExtrude","CAP_EDGE",EDGE,{"disambiguationData":[OSD([sQuery(id+"F0.wireOp",EDGE,"E1.top")])],"isStart":true});
            var Q189;
            Q189=makeQuery(id+"F1.opExtrude","SWEPT_EDGE",EDGE,{"disambiguationData":[OSD([sQuery(id+"F0.wireOp",EDGE,"E1.top"),sQuery(id+"F0.wireOp",EDGE,"E19.bottom"),sQuery(id+"F0.wireOp",EDGE,"E19.right")])]});
            var Q190;
            Q190=makeQuery(id+"F3.opExtrude","TWEAK_EDGE",EDGE,{"derivedFrom":[makeQuery(id+"F1.opExtrude","CAP_FACE",FACE,{"disambiguationData":[OSD([sQuery(id+"F0.wireOp",EDGE,"E8.top"),sQuery(id+"F0.wireOp",EDGE,"E10.right"),sQuery(id+"F0.wireOp",EDGE,"E13.right"),sQuery(id+"F0.wireOp",EDGE,"E20")])],"isStart":true}),makeQuery(id+"F2.imprint","IMPRINT",EDGE,{"derivedFrom":sQuery(id+"F2.wireOp",EDGE,"E52.top")})]});
            var Q191;
            Q191=makeQuery(id+"F3.opExtrude","TWEAK_EDGE",EDGE,{"derivedFrom":[makeQuery(id+"F1.opExtrude","CAP_FACE",FACE,{"disambiguationData":[OSD([sQuery(id+"F0.wireOp",EDGE,"E8.top"),sQuery(id+"F0.wireOp",EDGE,"E10.right"),sQuery(id+"F0.wireOp",EDGE,"E13.right"),sQuery(id+"F0.wireOp",EDGE,"E20")])],"isStart":true}),makeQuery(id+"F2.imprint","IMPRINT",EDGE,{"derivedFrom":sQuery(id+"F2.wireOp",EDGE,"E32.top")})]});
            var Q192;
            Q192=makeQuery(id+"F3.opExtrude","TWEAK_EDGE",EDGE,{"derivedFrom":[makeQuery(id+"F1.opExtrude","CAP_FACE",FACE,{"disambiguationData":[OSD([sQuery(id+"F0.wireOp",EDGE,"E8.top"),sQuery(id+"F0.wireOp",EDGE,"E10.right"),sQuery(id+"F0.wireOp",EDGE,"E13.right"),sQuery(id+"F0.wireOp",EDGE,"E20")])],"isStart":true}),makeQuery(id+"F2.imprint","IMPRINT",EDGE,{"derivedFrom":sQuery(id+"F2.wireOp",EDGE,"E47.top")})]});
            var Q193;
            Q193=makeQuery(id+"F3.opExtrude","TWEAK_EDGE",EDGE,{"derivedFrom":[makeQuery(id+"F1.opExtrude","CAP_FACE",FACE,{"disambiguationData":[OSD([sQuery(id+"F0.wireOp",EDGE,"E8.top"),sQuery(id+"F0.wireOp",EDGE,"E10.right"),sQuery(id+"F0.wireOp",EDGE,"E13.right"),sQuery(id+"F0.wireOp",EDGE,"E20")])],"isStart":true}),makeQuery(id+"F2.imprint","IMPRINT",EDGE,{"derivedFrom":sQuery(id+"F2.wireOp",EDGE,"E49.filletArc")}),makeQuery(id+"F2.imprint","IMPRINT",EDGE,{"derivedFrom":sQuery(id+"F2.wireOp",EDGE,"E50.filletArc")})]});
            var Q194;
            Q194=makeQuery(id+"F1.opExtrude","CAP_EDGE",EDGE,{"disambiguationData":[OSD([sQuery(id+"F0.wireOp",EDGE,"E0.top")])],"isStart":true});
            var Q195;
            Q195=makeQuery(id+"F1.opExtrude","SWEPT_EDGE",EDGE,{"disambiguationData":[OSD([sQuery(id+"F0.wireOp",EDGE,"E0.top"),sQuery(id+"F0.wireOp",EDGE,"E21.bottom"),sQuery(id+"F0.wireOp",EDGE,"E21.right")])]});
            var Q196;
            Q196=makeQuery(id+"F3.opExtrude","TWEAK_EDGE",EDGE,{"derivedFrom":[makeQuery(id+"F1.opExtrude","CAP_FACE",FACE,{"disambiguationData":[OSD([sQuery(id+"F0.wireOp",EDGE,"E8.top"),sQuery(id+"F0.wireOp",EDGE,"E10.right"),sQuery(id+"F0.wireOp",EDGE,"E13.right"),sQuery(id+"F0.wireOp",EDGE,"E20")])],"isStart":true}),makeQuery(id+"F2.imprint","IMPRINT",EDGE,{"derivedFrom":sQuery(id+"F2.wireOp",EDGE,"E57.top")})]});
            var Q197;
            Q197=makeQuery(id+"F3.opExtrude","TWEAK_EDGE",EDGE,{"derivedFrom":[makeQuery(id+"F1.opExtrude","CAP_FACE",FACE,{"disambiguationData":[OSD([sQuery(id+"F0.wireOp",EDGE,"E8.top"),sQuery(id+"F0.wireOp",EDGE,"E10.right"),sQuery(id+"F0.wireOp",EDGE,"E13.right"),sQuery(id+"F0.wireOp",EDGE,"E20")])],"isStart":true}),makeQuery(id+"F2.imprint","IMPRINT",EDGE,{"derivedFrom":sQuery(id+"F2.wireOp",EDGE,"E27.top")})]});
            var Q198;
            Q198=makeQuery(id+"F1.opExtrude","SWEPT_EDGE",EDGE,{"disambiguationData":[OSD([sQuery(id+"F0.wireOp",EDGE,"E6"),sQuery(id+"F0.wireOp",EDGE,"E14.bottom"),sQuery(id+"F0.wireOp",EDGE,"E14.right")])]});
            var Q199;
            Q199=makeQuery(id+"F1.opExtrude","CAP_EDGE",EDGE,{"disambiguationData":[OSD([sQuery(id+"F0.wireOp",EDGE,"E6")])],"isStart":true});
            var Q200;
            Q200=makeQuery(id+"F3.opExtrude","TWEAK_EDGE",EDGE,{"derivedFrom":[makeQuery(id+"F1.opExtrude","CAP_FACE",FACE,{"disambiguationData":[OSD([sQuery(id+"F0.wireOp",EDGE,"E8.top"),sQuery(id+"F0.wireOp",EDGE,"E10.right"),sQuery(id+"F0.wireOp",EDGE,"E13.right"),sQuery(id+"F0.wireOp",EDGE,"E20")])],"isStart":true}),makeQuery(id+"F2.imprint","IMPRINT",EDGE,{"derivedFrom":sQuery(id+"F2.wireOp",EDGE,"E29.filletArc")}),makeQuery(id+"F2.imprint","IMPRINT",EDGE,{"derivedFrom":sQuery(id+"F2.wireOp",EDGE,"E30.filletArc")})]});
            var Q201;
            Q201=makeQuery(id+"F3.opExtrude","TWEAK_EDGE",EDGE,{"derivedFrom":[makeQuery(id+"F1.opExtrude","CAP_FACE",FACE,{"disambiguationData":[OSD([sQuery(id+"F0.wireOp",EDGE,"E8.top"),sQuery(id+"F0.wireOp",EDGE,"E10.right"),sQuery(id+"F0.wireOp",EDGE,"E13.right"),sQuery(id+"F0.wireOp",EDGE,"E20")])],"isStart":true}),makeQuery(id+"F2.imprint","IMPRINT",EDGE,{"derivedFrom":sQuery(id+"F2.wireOp",EDGE,"E37.top")})]});
            var Q202;
            Q202=makeQuery(id+"F1.opExtrude","CAP_EDGE",EDGE,{"disambiguationData":[OSD([sQuery(id+"F0.wireOp",EDGE,"E8.top")])],"isStart":true});
            var Q203;
            Q203=makeQuery(id+"F3.opExtrude","TWEAK_EDGE",EDGE,{"derivedFrom":[makeQuery(id+"F1.opExtrude","CAP_FACE",FACE,{"disambiguationData":[OSD([sQuery(id+"F0.wireOp",EDGE,"E8.top"),sQuery(id+"F0.wireOp",EDGE,"E10.right"),sQuery(id+"F0.wireOp",EDGE,"E13.right"),sQuery(id+"F0.wireOp",EDGE,"E20")])],"isStart":true}),makeQuery(id+"F2.imprint","IMPRINT",EDGE,{"derivedFrom":sQuery(id+"F2.wireOp",EDGE,"E22.top")})]});
            var Q204;
            Q204=makeQuery(id+"F1.opExtrude","SWEPT_EDGE",EDGE,{"disambiguationData":[OSD([sQuery(id+"F0.wireOp",EDGE,"E8.top"),sQuery(id+"F0.wireOp",EDGE,"E13.bottom"),sQuery(id+"F0.wireOp",EDGE,"E13.right")])]});
            var Q205;
            {var subQ0=sQuery(id+"F0.wireOp",EDGE,"E10.right");var subQ3=sQuery(id+"F0.wireOp",EDGE,"E8.top");Q205=makeQuery(id+"F3.boolean.opBoolean","SPLIT",EDGE,{"disambiguationData":[TD([makeQuery(id+"F1.opExtrude","SWEPT_FACE",FACE,{"disambiguationData":[OSD([subQ3])]})])],"derivedFrom":makeQuery(id+"F1.opExtrude","CAP_EDGE",EDGE,{"disambiguationData":[OSD([subQ0])],"isStart":true})});}
            var Q206;
            Q206=makeQuery(id+"F3.opExtrude","TWEAK_EDGE",EDGE,{"derivedFrom":[makeQuery(id+"F1.opExtrude","CAP_FACE",FACE,{"disambiguationData":[OSD([sQuery(id+"F0.wireOp",EDGE,"E8.top"),sQuery(id+"F0.wireOp",EDGE,"E10.right"),sQuery(id+"F0.wireOp",EDGE,"E13.right"),sQuery(id+"F0.wireOp",EDGE,"E20")])],"isStart":true}),makeQuery(id+"F2.imprint","IMPRINT",EDGE,{"derivedFrom":sQuery(id+"F2.wireOp",EDGE,"E44.filletArc")}),makeQuery(id+"F2.imprint","IMPRINT",EDGE,{"derivedFrom":sQuery(id+"F2.wireOp",EDGE,"E45.filletArc")})]});
            var Q207;
            Q207=makeQuery(id+"F3.opExtrude","TWEAK_EDGE",EDGE,{"derivedFrom":[makeQuery(id+"F1.opExtrude","CAP_FACE",FACE,{"disambiguationData":[OSD([sQuery(id+"F0.wireOp",EDGE,"E8.top"),sQuery(id+"F0.wireOp",EDGE,"E10.right"),sQuery(id+"F0.wireOp",EDGE,"E13.right"),sQuery(id+"F0.wireOp",EDGE,"E20")])],"isStart":true}),makeQuery(id+"F2.imprint","IMPRINT",EDGE,{"derivedFrom":sQuery(id+"F2.wireOp",EDGE,"E42.top")})]});
            fillet(context, id + "F5", {"entities" : qUnion([Q0, Q1, Q2, Q3, Q4, Q5, Q6, Q7, Q8, Q9, Q10, Q11, Q12, Q13, Q14, Q15, Q16, Q17, Q18, Q19, Q20, Q21, Q22, Q23, Q24, Q25, Q26, Q27, Q28, Q29, Q30, Q31, Q32, Q33, Q34, Q35, Q36, Q37, Q38, Q39, Q40, Q41, Q42, Q43, Q44, Q45, Q46, Q47, Q48, Q49, Q50, Q51, Q52, Q53, Q54, Q55, Q56, Q57, Q58, Q59, Q60, Q61, Q62, Q63, Q64, Q65, Q66, Q67, Q68, Q69, Q70, Q71, Q72, Q73, Q74, Q75, Q76, Q77, Q78, Q79, Q80, Q81, Q82, Q83, Q84, Q85, Q86, Q87, Q88, Q89, Q90, Q91, Q92, Q93, Q94, Q95, Q96, Q97, Q98, Q99, Q100, Q101, Q102, Q103, Q104, Q105, Q106, Q107, Q108, Q109, Q110, Q111, Q112, Q113, Q114, Q115, Q116, Q117, Q118, Q119, Q120, Q121, Q122, Q123, Q124, Q125, Q126, Q127, Q128, Q129, Q130, Q131, Q132, Q133, Q134, Q135, Q136, Q137, Q138, Q139, Q140, Q141, Q142, Q143, Q144, Q145, Q146, Q147, Q148, Q149, Q150, Q151, Q152, Q153, Q154, Q155, Q156, Q157, Q158, Q159, Q160, Q161, Q162, Q163, Q164, Q165, Q166, Q167, Q168, Q169, Q170, Q171, Q172, Q173, Q174, Q175, Q176, Q177, Q178, Q179, Q180, Q181, Q182, Q183, Q184, Q185, Q186, Q187, Q188, Q189, Q190, Q191, Q192, Q193, Q194, Q195, Q196, Q197, Q198, Q199, Q200, Q201, Q202, Q203, Q204, Q205, Q206, Q207]), "radius" : 1.5 * mm, "tangentPropagation" : true, "allowEdgeOverflow" : false});
        }
    });
